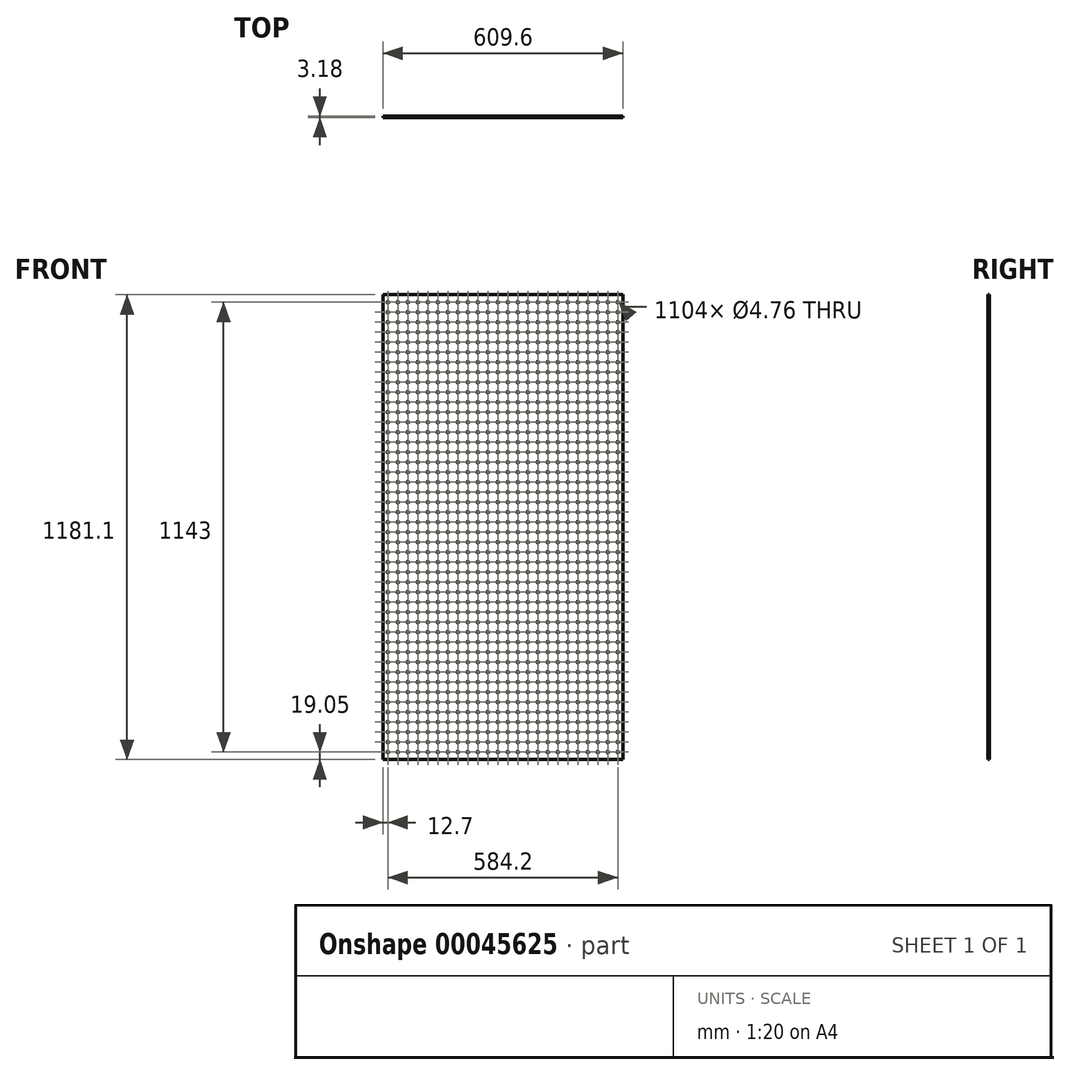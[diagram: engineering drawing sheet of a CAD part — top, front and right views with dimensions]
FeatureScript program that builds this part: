
annotation { "Feature Type Name" : "Feature", "Feature Type Description" : "" }
export const myFeature = defineFeature(function(context is Context, id is Id, definition is map)
    precondition{}
    {
        {
            var Q0;
            Q0=qCreatedBy(makeId("Front.planeOp"),FACE);
            var sketch = newSketch(context, id + "F0", { "sketchPlane" : qUnion([Q0])});
            skLineSegment(sketch, "E0.bottom", {"start": v(-609.6, 0) * mm, "end": v(0, 0) * mm});
            skLineSegment(sketch, "E0.top", {"start": v(-609.6, -1181.1) * mm, "end": v(0, -1181.1) * mm});
            skLineSegment(sketch, "E0.left", {"start": v(-609.6, 0) * mm, "end": v(-609.6, -1181.1) * mm});
            skLineSegment(sketch, "E0.right", {"start": v(0, 0) * mm, "end": v(0, -1181.1) * mm});
            skCircle(sketch, "E1", {"center": v(-596.9, -19.05) * mm, "radius": 2.38 * mm});
            skCircle(sketch, "E2.0.1.0", {"center": v(-596.9, -44.45) * mm, "radius": 2.38 * mm});
            skCircle(sketch, "E2.0.2.0", {"center": v(-596.9, -69.85) * mm, "radius": 2.38 * mm});
            skCircle(sketch, "E2.0.3.0", {"center": v(-596.9, -95.25) * mm, "radius": 2.38 * mm});
            skCircle(sketch, "E2.0.4.0", {"center": v(-596.9, -120.65) * mm, "radius": 2.38 * mm});
            skCircle(sketch, "E2.0.5.0", {"center": v(-596.9, -146.05) * mm, "radius": 2.38 * mm});
            skCircle(sketch, "E2.0.6.0", {"center": v(-596.9, -171.45) * mm, "radius": 2.38 * mm});
            skCircle(sketch, "E2.0.7.0", {"center": v(-596.9, -196.85) * mm, "radius": 2.38 * mm});
            skCircle(sketch, "E2.0.8.0", {"center": v(-596.9, -222.25) * mm, "radius": 2.38 * mm});
            skCircle(sketch, "E2.0.9.0", {"center": v(-596.9, -247.65) * mm, "radius": 2.38 * mm});
            skCircle(sketch, "E2.1.0.0", {"center": v(-571.5, -19.05) * mm, "radius": 2.38 * mm});
            skCircle(sketch, "E2.1.1.0", {"center": v(-571.5, -44.45) * mm, "radius": 2.38 * mm});
            skCircle(sketch, "E2.1.2.0", {"center": v(-571.5, -69.85) * mm, "radius": 2.38 * mm});
            skCircle(sketch, "E2.1.3.0", {"center": v(-571.5, -95.25) * mm, "radius": 2.38 * mm});
            skCircle(sketch, "E2.1.4.0", {"center": v(-571.5, -120.65) * mm, "radius": 2.38 * mm});
            skCircle(sketch, "E2.1.5.0", {"center": v(-571.5, -146.05) * mm, "radius": 2.38 * mm});
            skCircle(sketch, "E2.1.6.0", {"center": v(-571.5, -171.45) * mm, "radius": 2.38 * mm});
            skCircle(sketch, "E2.1.7.0", {"center": v(-571.5, -196.85) * mm, "radius": 2.38 * mm});
            skCircle(sketch, "E2.1.8.0", {"center": v(-571.5, -222.25) * mm, "radius": 2.38 * mm});
            skCircle(sketch, "E2.1.9.0", {"center": v(-571.5, -247.65) * mm, "radius": 2.38 * mm});
            skCircle(sketch, "E2.2.0.0", {"center": v(-546.1, -19.05) * mm, "radius": 2.38 * mm});
            skCircle(sketch, "E2.2.1.0", {"center": v(-546.1, -44.45) * mm, "radius": 2.38 * mm});
            skCircle(sketch, "E2.2.2.0", {"center": v(-546.1, -69.85) * mm, "radius": 2.38 * mm});
            skCircle(sketch, "E2.2.3.0", {"center": v(-546.1, -95.25) * mm, "radius": 2.38 * mm});
            skCircle(sketch, "E2.2.4.0", {"center": v(-546.1, -120.65) * mm, "radius": 2.38 * mm});
            skCircle(sketch, "E2.2.5.0", {"center": v(-546.1, -146.05) * mm, "radius": 2.38 * mm});
            skCircle(sketch, "E2.2.6.0", {"center": v(-546.1, -171.45) * mm, "radius": 2.38 * mm});
            skCircle(sketch, "E2.2.7.0", {"center": v(-546.1, -196.85) * mm, "radius": 2.38 * mm});
            skCircle(sketch, "E2.2.8.0", {"center": v(-546.1, -222.25) * mm, "radius": 2.38 * mm});
            skCircle(sketch, "E2.2.9.0", {"center": v(-546.1, -247.65) * mm, "radius": 2.38 * mm});
            skCircle(sketch, "E2.3.0.0", {"center": v(-520.7, -19.05) * mm, "radius": 2.38 * mm});
            skCircle(sketch, "E2.3.1.0", {"center": v(-520.7, -44.45) * mm, "radius": 2.38 * mm});
            skCircle(sketch, "E2.3.2.0", {"center": v(-520.7, -69.85) * mm, "radius": 2.38 * mm});
            skCircle(sketch, "E2.3.3.0", {"center": v(-520.7, -95.25) * mm, "radius": 2.38 * mm});
            skCircle(sketch, "E2.3.4.0", {"center": v(-520.7, -120.65) * mm, "radius": 2.38 * mm});
            skCircle(sketch, "E2.3.5.0", {"center": v(-520.7, -146.05) * mm, "radius": 2.38 * mm});
            skCircle(sketch, "E2.3.6.0", {"center": v(-520.7, -171.45) * mm, "radius": 2.38 * mm});
            skCircle(sketch, "E2.3.7.0", {"center": v(-520.7, -196.85) * mm, "radius": 2.38 * mm});
            skCircle(sketch, "E2.3.8.0", {"center": v(-520.7, -222.25) * mm, "radius": 2.38 * mm});
            skCircle(sketch, "E2.3.9.0", {"center": v(-520.7, -247.65) * mm, "radius": 2.38 * mm});
            skCircle(sketch, "E2.4.0.0", {"center": v(-495.3, -19.05) * mm, "radius": 2.38 * mm});
            skCircle(sketch, "E2.4.1.0", {"center": v(-495.3, -44.45) * mm, "radius": 2.38 * mm});
            skCircle(sketch, "E2.4.2.0", {"center": v(-495.3, -69.85) * mm, "radius": 2.38 * mm});
            skCircle(sketch, "E2.4.3.0", {"center": v(-495.3, -95.25) * mm, "radius": 2.38 * mm});
            skCircle(sketch, "E2.4.4.0", {"center": v(-495.3, -120.65) * mm, "radius": 2.38 * mm});
            skCircle(sketch, "E2.4.5.0", {"center": v(-495.3, -146.05) * mm, "radius": 2.38 * mm});
            skCircle(sketch, "E2.4.6.0", {"center": v(-495.3, -171.45) * mm, "radius": 2.38 * mm});
            skCircle(sketch, "E2.4.7.0", {"center": v(-495.3, -196.85) * mm, "radius": 2.38 * mm});
            skCircle(sketch, "E2.4.8.0", {"center": v(-495.3, -222.25) * mm, "radius": 2.38 * mm});
            skCircle(sketch, "E2.4.9.0", {"center": v(-495.3, -247.65) * mm, "radius": 2.38 * mm});
            skCircle(sketch, "E2.5.0.0", {"center": v(-469.9, -19.05) * mm, "radius": 2.38 * mm});
            skCircle(sketch, "E2.5.1.0", {"center": v(-469.9, -44.45) * mm, "radius": 2.38 * mm});
            skCircle(sketch, "E2.5.2.0", {"center": v(-469.9, -69.85) * mm, "radius": 2.38 * mm});
            skCircle(sketch, "E2.5.3.0", {"center": v(-469.9, -95.25) * mm, "radius": 2.38 * mm});
            skCircle(sketch, "E2.5.4.0", {"center": v(-469.9, -120.65) * mm, "radius": 2.38 * mm});
            skCircle(sketch, "E2.5.5.0", {"center": v(-469.9, -146.05) * mm, "radius": 2.38 * mm});
            skCircle(sketch, "E2.5.6.0", {"center": v(-469.9, -171.45) * mm, "radius": 2.38 * mm});
            skCircle(sketch, "E2.5.7.0", {"center": v(-469.9, -196.85) * mm, "radius": 2.38 * mm});
            skCircle(sketch, "E2.5.8.0", {"center": v(-469.9, -222.25) * mm, "radius": 2.38 * mm});
            skCircle(sketch, "E2.5.9.0", {"center": v(-469.9, -247.65) * mm, "radius": 2.38 * mm});
            skCircle(sketch, "E2.6.0.0", {"center": v(-444.5, -19.05) * mm, "radius": 2.38 * mm});
            skCircle(sketch, "E2.6.1.0", {"center": v(-444.5, -44.45) * mm, "radius": 2.38 * mm});
            skCircle(sketch, "E2.6.2.0", {"center": v(-444.5, -69.85) * mm, "radius": 2.38 * mm});
            skCircle(sketch, "E2.6.3.0", {"center": v(-444.5, -95.25) * mm, "radius": 2.38 * mm});
            skCircle(sketch, "E2.6.4.0", {"center": v(-444.5, -120.65) * mm, "radius": 2.38 * mm});
            skCircle(sketch, "E2.6.5.0", {"center": v(-444.5, -146.05) * mm, "radius": 2.38 * mm});
            skCircle(sketch, "E2.6.6.0", {"center": v(-444.5, -171.45) * mm, "radius": 2.38 * mm});
            skCircle(sketch, "E2.6.7.0", {"center": v(-444.5, -196.85) * mm, "radius": 2.38 * mm});
            skCircle(sketch, "E2.6.8.0", {"center": v(-444.5, -222.25) * mm, "radius": 2.38 * mm});
            skCircle(sketch, "E2.6.9.0", {"center": v(-444.5, -247.65) * mm, "radius": 2.38 * mm});
            skCircle(sketch, "E2.7.0.0", {"center": v(-419.1, -19.05) * mm, "radius": 2.38 * mm});
            skCircle(sketch, "E2.7.1.0", {"center": v(-419.1, -44.45) * mm, "radius": 2.38 * mm});
            skCircle(sketch, "E2.7.2.0", {"center": v(-419.1, -69.85) * mm, "radius": 2.38 * mm});
            skCircle(sketch, "E2.7.3.0", {"center": v(-419.1, -95.25) * mm, "radius": 2.38 * mm});
            skCircle(sketch, "E2.7.4.0", {"center": v(-419.1, -120.65) * mm, "radius": 2.38 * mm});
            skCircle(sketch, "E2.7.5.0", {"center": v(-419.1, -146.05) * mm, "radius": 2.38 * mm});
            skCircle(sketch, "E2.7.6.0", {"center": v(-419.1, -171.45) * mm, "radius": 2.38 * mm});
            skCircle(sketch, "E2.7.7.0", {"center": v(-419.1, -196.85) * mm, "radius": 2.38 * mm});
            skCircle(sketch, "E2.7.8.0", {"center": v(-419.1, -222.25) * mm, "radius": 2.38 * mm});
            skCircle(sketch, "E2.7.9.0", {"center": v(-419.1, -247.65) * mm, "radius": 2.38 * mm});
            skCircle(sketch, "E2.8.0.0", {"center": v(-393.7, -19.05) * mm, "radius": 2.38 * mm});
            skCircle(sketch, "E2.8.1.0", {"center": v(-393.7, -44.45) * mm, "radius": 2.38 * mm});
            skCircle(sketch, "E2.8.2.0", {"center": v(-393.7, -69.85) * mm, "radius": 2.38 * mm});
            skCircle(sketch, "E2.8.3.0", {"center": v(-393.7, -95.25) * mm, "radius": 2.38 * mm});
            skCircle(sketch, "E2.8.4.0", {"center": v(-393.7, -120.65) * mm, "radius": 2.38 * mm});
            skCircle(sketch, "E2.8.5.0", {"center": v(-393.7, -146.05) * mm, "radius": 2.38 * mm});
            skCircle(sketch, "E2.8.6.0", {"center": v(-393.7, -171.45) * mm, "radius": 2.38 * mm});
            skCircle(sketch, "E2.8.7.0", {"center": v(-393.7, -196.85) * mm, "radius": 2.38 * mm});
            skCircle(sketch, "E2.8.8.0", {"center": v(-393.7, -222.25) * mm, "radius": 2.38 * mm});
            skCircle(sketch, "E2.8.9.0", {"center": v(-393.7, -247.65) * mm, "radius": 2.38 * mm});
            skCircle(sketch, "E2.9.0.0", {"center": v(-368.3, -19.05) * mm, "radius": 2.38 * mm});
            skCircle(sketch, "E2.9.1.0", {"center": v(-368.3, -44.45) * mm, "radius": 2.38 * mm});
            skCircle(sketch, "E2.9.2.0", {"center": v(-368.3, -69.85) * mm, "radius": 2.38 * mm});
            skCircle(sketch, "E2.9.3.0", {"center": v(-368.3, -95.25) * mm, "radius": 2.38 * mm});
            skCircle(sketch, "E2.9.4.0", {"center": v(-368.3, -120.65) * mm, "radius": 2.38 * mm});
            skCircle(sketch, "E2.9.5.0", {"center": v(-368.3, -146.05) * mm, "radius": 2.38 * mm});
            skCircle(sketch, "E2.9.6.0", {"center": v(-368.3, -171.45) * mm, "radius": 2.38 * mm});
            skCircle(sketch, "E2.9.7.0", {"center": v(-368.3, -196.85) * mm, "radius": 2.38 * mm});
            skCircle(sketch, "E2.9.8.0", {"center": v(-368.3, -222.25) * mm, "radius": 2.38 * mm});
            skCircle(sketch, "E2.9.9.0", {"center": v(-368.3, -247.65) * mm, "radius": 2.38 * mm});
            skLineSegment(sketch, "E2.direction1", {"start": v(-596.9, -19.05) * mm, "end": v(-571.5, -19.05) * mm, "construction": true});
            skLineSegment(sketch, "E2.direction2", {"start": v(-596.9, -19.05) * mm, "end": v(-596.9, -44.45) * mm, "construction": true});
            skCircle(sketch, "E3.0.10.0", {"center": v(-342.9, -19.05) * mm, "radius": 2.38 * mm});
            skCircle(sketch, "E3.0.10.1", {"center": v(-342.9, -44.45) * mm, "radius": 2.38 * mm});
            skCircle(sketch, "E3.0.10.2", {"center": v(-342.9, -69.85) * mm, "radius": 2.38 * mm});
            skCircle(sketch, "E3.0.10.3", {"center": v(-342.9, -95.25) * mm, "radius": 2.38 * mm});
            skCircle(sketch, "E3.0.10.4", {"center": v(-342.9, -120.65) * mm, "radius": 2.38 * mm});
            skCircle(sketch, "E3.0.10.5", {"center": v(-342.9, -146.05) * mm, "radius": 2.38 * mm});
            skCircle(sketch, "E3.0.10.6", {"center": v(-342.9, -171.45) * mm, "radius": 2.38 * mm});
            skCircle(sketch, "E3.0.10.7", {"center": v(-342.9, -196.85) * mm, "radius": 2.38 * mm});
            skCircle(sketch, "E3.0.10.8", {"center": v(-342.9, -222.25) * mm, "radius": 2.38 * mm});
            skCircle(sketch, "E3.0.10.9", {"center": v(-342.9, -247.65) * mm, "radius": 2.38 * mm});
            skCircle(sketch, "E3.0.11.0", {"center": v(-317.5, -19.05) * mm, "radius": 2.38 * mm});
            skCircle(sketch, "E3.0.11.1", {"center": v(-317.5, -44.45) * mm, "radius": 2.38 * mm});
            skCircle(sketch, "E3.0.11.2", {"center": v(-317.5, -69.85) * mm, "radius": 2.38 * mm});
            skCircle(sketch, "E3.0.11.3", {"center": v(-317.5, -95.25) * mm, "radius": 2.38 * mm});
            skCircle(sketch, "E3.0.11.4", {"center": v(-317.5, -120.65) * mm, "radius": 2.38 * mm});
            skCircle(sketch, "E3.0.11.5", {"center": v(-317.5, -146.05) * mm, "radius": 2.38 * mm});
            skCircle(sketch, "E3.0.11.6", {"center": v(-317.5, -171.45) * mm, "radius": 2.38 * mm});
            skCircle(sketch, "E3.0.11.7", {"center": v(-317.5, -196.85) * mm, "radius": 2.38 * mm});
            skCircle(sketch, "E3.0.11.8", {"center": v(-317.5, -222.25) * mm, "radius": 2.38 * mm});
            skCircle(sketch, "E3.0.11.9", {"center": v(-317.5, -247.65) * mm, "radius": 2.38 * mm});
            skCircle(sketch, "E3.0.12.0", {"center": v(-292.1, -19.05) * mm, "radius": 2.38 * mm});
            skCircle(sketch, "E3.0.12.1", {"center": v(-292.1, -44.45) * mm, "radius": 2.38 * mm});
            skCircle(sketch, "E3.0.12.2", {"center": v(-292.1, -69.85) * mm, "radius": 2.38 * mm});
            skCircle(sketch, "E3.0.12.3", {"center": v(-292.1, -95.25) * mm, "radius": 2.38 * mm});
            skCircle(sketch, "E3.0.12.4", {"center": v(-292.1, -120.65) * mm, "radius": 2.38 * mm});
            skCircle(sketch, "E3.0.12.5", {"center": v(-292.1, -146.05) * mm, "radius": 2.38 * mm});
            skCircle(sketch, "E3.0.12.6", {"center": v(-292.1, -171.45) * mm, "radius": 2.38 * mm});
            skCircle(sketch, "E3.0.12.7", {"center": v(-292.1, -196.85) * mm, "radius": 2.38 * mm});
            skCircle(sketch, "E3.0.12.8", {"center": v(-292.1, -222.25) * mm, "radius": 2.38 * mm});
            skCircle(sketch, "E3.0.12.9", {"center": v(-292.1, -247.65) * mm, "radius": 2.38 * mm});
            skCircle(sketch, "E3.0.13.0", {"center": v(-266.7, -19.05) * mm, "radius": 2.38 * mm});
            skCircle(sketch, "E3.0.13.1", {"center": v(-266.7, -44.45) * mm, "radius": 2.38 * mm});
            skCircle(sketch, "E3.0.13.2", {"center": v(-266.7, -69.85) * mm, "radius": 2.38 * mm});
            skCircle(sketch, "E3.0.13.3", {"center": v(-266.7, -95.25) * mm, "radius": 2.38 * mm});
            skCircle(sketch, "E3.0.13.4", {"center": v(-266.7, -120.65) * mm, "radius": 2.38 * mm});
            skCircle(sketch, "E3.0.13.5", {"center": v(-266.7, -146.05) * mm, "radius": 2.38 * mm});
            skCircle(sketch, "E3.0.13.6", {"center": v(-266.7, -171.45) * mm, "radius": 2.38 * mm});
            skCircle(sketch, "E3.0.13.7", {"center": v(-266.7, -196.85) * mm, "radius": 2.38 * mm});
            skCircle(sketch, "E3.0.13.8", {"center": v(-266.7, -222.25) * mm, "radius": 2.38 * mm});
            skCircle(sketch, "E3.0.13.9", {"center": v(-266.7, -247.65) * mm, "radius": 2.38 * mm});
            skCircle(sketch, "E3.0.14.0", {"center": v(-241.3, -19.05) * mm, "radius": 2.38 * mm});
            skCircle(sketch, "E3.0.14.1", {"center": v(-241.3, -44.45) * mm, "radius": 2.38 * mm});
            skCircle(sketch, "E3.0.14.2", {"center": v(-241.3, -69.85) * mm, "radius": 2.38 * mm});
            skCircle(sketch, "E3.0.14.3", {"center": v(-241.3, -95.25) * mm, "radius": 2.38 * mm});
            skCircle(sketch, "E3.0.14.4", {"center": v(-241.3, -120.65) * mm, "radius": 2.38 * mm});
            skCircle(sketch, "E3.0.14.5", {"center": v(-241.3, -146.05) * mm, "radius": 2.38 * mm});
            skCircle(sketch, "E3.0.14.6", {"center": v(-241.3, -171.45) * mm, "radius": 2.38 * mm});
            skCircle(sketch, "E3.0.14.7", {"center": v(-241.3, -196.85) * mm, "radius": 2.38 * mm});
            skCircle(sketch, "E3.0.14.8", {"center": v(-241.3, -222.25) * mm, "radius": 2.38 * mm});
            skCircle(sketch, "E3.0.14.9", {"center": v(-241.3, -247.65) * mm, "radius": 2.38 * mm});
            skCircle(sketch, "E4.0.15.0", {"center": v(-215.9, -19.05) * mm, "radius": 2.38 * mm});
            skCircle(sketch, "E4.0.15.1", {"center": v(-215.9, -44.45) * mm, "radius": 2.38 * mm});
            skCircle(sketch, "E4.0.15.2", {"center": v(-215.9, -69.85) * mm, "radius": 2.38 * mm});
            skCircle(sketch, "E4.0.15.3", {"center": v(-215.9, -95.25) * mm, "radius": 2.38 * mm});
            skCircle(sketch, "E4.0.15.4", {"center": v(-215.9, -120.65) * mm, "radius": 2.38 * mm});
            skCircle(sketch, "E4.0.15.5", {"center": v(-215.9, -146.05) * mm, "radius": 2.38 * mm});
            skCircle(sketch, "E4.0.15.6", {"center": v(-215.9, -171.45) * mm, "radius": 2.38 * mm});
            skCircle(sketch, "E4.0.15.7", {"center": v(-215.9, -196.85) * mm, "radius": 2.38 * mm});
            skCircle(sketch, "E4.0.15.8", {"center": v(-215.9, -222.25) * mm, "radius": 2.38 * mm});
            skCircle(sketch, "E4.0.15.9", {"center": v(-215.9, -247.65) * mm, "radius": 2.38 * mm});
            skCircle(sketch, "E4.0.16.0", {"center": v(-190.5, -19.05) * mm, "radius": 2.38 * mm});
            skCircle(sketch, "E4.0.16.1", {"center": v(-190.5, -44.45) * mm, "radius": 2.38 * mm});
            skCircle(sketch, "E4.0.16.2", {"center": v(-190.5, -69.85) * mm, "radius": 2.38 * mm});
            skCircle(sketch, "E4.0.16.3", {"center": v(-190.5, -95.25) * mm, "radius": 2.38 * mm});
            skCircle(sketch, "E4.0.16.4", {"center": v(-190.5, -120.65) * mm, "radius": 2.38 * mm});
            skCircle(sketch, "E4.0.16.5", {"center": v(-190.5, -146.05) * mm, "radius": 2.38 * mm});
            skCircle(sketch, "E4.0.16.6", {"center": v(-190.5, -171.45) * mm, "radius": 2.38 * mm});
            skCircle(sketch, "E4.0.16.7", {"center": v(-190.5, -196.85) * mm, "radius": 2.38 * mm});
            skCircle(sketch, "E4.0.16.8", {"center": v(-190.5, -222.25) * mm, "radius": 2.38 * mm});
            skCircle(sketch, "E4.0.16.9", {"center": v(-190.5, -247.65) * mm, "radius": 2.38 * mm});
            skCircle(sketch, "E4.0.17.0", {"center": v(-165.1, -19.05) * mm, "radius": 2.38 * mm});
            skCircle(sketch, "E4.0.17.1", {"center": v(-165.1, -44.45) * mm, "radius": 2.38 * mm});
            skCircle(sketch, "E4.0.17.2", {"center": v(-165.1, -69.85) * mm, "radius": 2.38 * mm});
            skCircle(sketch, "E4.0.17.3", {"center": v(-165.1, -95.25) * mm, "radius": 2.38 * mm});
            skCircle(sketch, "E4.0.17.4", {"center": v(-165.1, -120.65) * mm, "radius": 2.38 * mm});
            skCircle(sketch, "E4.0.17.5", {"center": v(-165.1, -146.05) * mm, "radius": 2.38 * mm});
            skCircle(sketch, "E4.0.17.6", {"center": v(-165.1, -171.45) * mm, "radius": 2.38 * mm});
            skCircle(sketch, "E4.0.17.7", {"center": v(-165.1, -196.85) * mm, "radius": 2.38 * mm});
            skCircle(sketch, "E4.0.17.8", {"center": v(-165.1, -222.25) * mm, "radius": 2.38 * mm});
            skCircle(sketch, "E4.0.17.9", {"center": v(-165.1, -247.65) * mm, "radius": 2.38 * mm});
            skCircle(sketch, "E4.0.18.0", {"center": v(-139.7, -19.05) * mm, "radius": 2.38 * mm});
            skCircle(sketch, "E4.0.18.1", {"center": v(-139.7, -44.45) * mm, "radius": 2.38 * mm});
            skCircle(sketch, "E4.0.18.2", {"center": v(-139.7, -69.85) * mm, "radius": 2.38 * mm});
            skCircle(sketch, "E4.0.18.3", {"center": v(-139.7, -95.25) * mm, "radius": 2.38 * mm});
            skCircle(sketch, "E4.0.18.4", {"center": v(-139.7, -120.65) * mm, "radius": 2.38 * mm});
            skCircle(sketch, "E4.0.18.5", {"center": v(-139.7, -146.05) * mm, "radius": 2.38 * mm});
            skCircle(sketch, "E4.0.18.6", {"center": v(-139.7, -171.45) * mm, "radius": 2.38 * mm});
            skCircle(sketch, "E4.0.18.7", {"center": v(-139.7, -196.85) * mm, "radius": 2.38 * mm});
            skCircle(sketch, "E4.0.18.8", {"center": v(-139.7, -222.25) * mm, "radius": 2.38 * mm});
            skCircle(sketch, "E4.0.18.9", {"center": v(-139.7, -247.65) * mm, "radius": 2.38 * mm});
            skCircle(sketch, "E4.0.19.0", {"center": v(-114.3, -19.05) * mm, "radius": 2.38 * mm});
            skCircle(sketch, "E4.0.19.1", {"center": v(-114.3, -44.45) * mm, "radius": 2.38 * mm});
            skCircle(sketch, "E4.0.19.2", {"center": v(-114.3, -69.85) * mm, "radius": 2.38 * mm});
            skCircle(sketch, "E4.0.19.3", {"center": v(-114.3, -95.25) * mm, "radius": 2.38 * mm});
            skCircle(sketch, "E4.0.19.4", {"center": v(-114.3, -120.65) * mm, "radius": 2.38 * mm});
            skCircle(sketch, "E4.0.19.5", {"center": v(-114.3, -146.05) * mm, "radius": 2.38 * mm});
            skCircle(sketch, "E4.0.19.6", {"center": v(-114.3, -171.45) * mm, "radius": 2.38 * mm});
            skCircle(sketch, "E4.0.19.7", {"center": v(-114.3, -196.85) * mm, "radius": 2.38 * mm});
            skCircle(sketch, "E4.0.19.8", {"center": v(-114.3, -222.25) * mm, "radius": 2.38 * mm});
            skCircle(sketch, "E4.0.19.9", {"center": v(-114.3, -247.65) * mm, "radius": 2.38 * mm});
            skCircle(sketch, "E4.0.20.0", {"center": v(-88.9, -19.05) * mm, "radius": 2.38 * mm});
            skCircle(sketch, "E4.0.20.1", {"center": v(-88.9, -44.45) * mm, "radius": 2.38 * mm});
            skCircle(sketch, "E4.0.20.2", {"center": v(-88.9, -69.85) * mm, "radius": 2.38 * mm});
            skCircle(sketch, "E4.0.20.3", {"center": v(-88.9, -95.25) * mm, "radius": 2.38 * mm});
            skCircle(sketch, "E4.0.20.4", {"center": v(-88.9, -120.65) * mm, "radius": 2.38 * mm});
            skCircle(sketch, "E4.0.20.5", {"center": v(-88.9, -146.05) * mm, "radius": 2.38 * mm});
            skCircle(sketch, "E4.0.20.6", {"center": v(-88.9, -171.45) * mm, "radius": 2.38 * mm});
            skCircle(sketch, "E4.0.20.7", {"center": v(-88.9, -196.85) * mm, "radius": 2.38 * mm});
            skCircle(sketch, "E4.0.20.8", {"center": v(-88.9, -222.25) * mm, "radius": 2.38 * mm});
            skCircle(sketch, "E4.0.20.9", {"center": v(-88.9, -247.65) * mm, "radius": 2.38 * mm});
            skCircle(sketch, "E4.0.21.0", {"center": v(-63.5, -19.05) * mm, "radius": 2.38 * mm});
            skCircle(sketch, "E4.0.21.1", {"center": v(-63.5, -44.45) * mm, "radius": 2.38 * mm});
            skCircle(sketch, "E4.0.21.2", {"center": v(-63.5, -69.85) * mm, "radius": 2.38 * mm});
            skCircle(sketch, "E4.0.21.3", {"center": v(-63.5, -95.25) * mm, "radius": 2.38 * mm});
            skCircle(sketch, "E4.0.21.4", {"center": v(-63.5, -120.65) * mm, "radius": 2.38 * mm});
            skCircle(sketch, "E4.0.21.5", {"center": v(-63.5, -146.05) * mm, "radius": 2.38 * mm});
            skCircle(sketch, "E4.0.21.6", {"center": v(-63.5, -171.45) * mm, "radius": 2.38 * mm});
            skCircle(sketch, "E4.0.21.7", {"center": v(-63.5, -196.85) * mm, "radius": 2.38 * mm});
            skCircle(sketch, "E4.0.21.8", {"center": v(-63.5, -222.25) * mm, "radius": 2.38 * mm});
            skCircle(sketch, "E4.0.21.9", {"center": v(-63.5, -247.65) * mm, "radius": 2.38 * mm});
            skCircle(sketch, "E5.0.22.0", {"center": v(-38.1, -19.05) * mm, "radius": 2.38 * mm});
            skCircle(sketch, "E5.0.22.1", {"center": v(-38.1, -44.45) * mm, "radius": 2.38 * mm});
            skCircle(sketch, "E5.0.22.2", {"center": v(-38.1, -69.85) * mm, "radius": 2.38 * mm});
            skCircle(sketch, "E5.0.22.3", {"center": v(-38.1, -95.25) * mm, "radius": 2.38 * mm});
            skCircle(sketch, "E5.0.22.4", {"center": v(-38.1, -120.65) * mm, "radius": 2.38 * mm});
            skCircle(sketch, "E5.0.22.5", {"center": v(-38.1, -146.05) * mm, "radius": 2.38 * mm});
            skCircle(sketch, "E5.0.22.6", {"center": v(-38.1, -171.45) * mm, "radius": 2.38 * mm});
            skCircle(sketch, "E5.0.22.7", {"center": v(-38.1, -196.85) * mm, "radius": 2.38 * mm});
            skCircle(sketch, "E5.0.22.8", {"center": v(-38.1, -222.25) * mm, "radius": 2.38 * mm});
            skCircle(sketch, "E5.0.22.9", {"center": v(-38.1, -247.65) * mm, "radius": 2.38 * mm});
            skCircle(sketch, "E6.0.23.0", {"center": v(-12.7, -19.05) * mm, "radius": 2.38 * mm});
            skCircle(sketch, "E6.0.23.1", {"center": v(-12.7, -44.45) * mm, "radius": 2.38 * mm});
            skCircle(sketch, "E6.0.23.2", {"center": v(-12.7, -69.85) * mm, "radius": 2.38 * mm});
            skCircle(sketch, "E6.0.23.3", {"center": v(-12.7, -95.25) * mm, "radius": 2.38 * mm});
            skCircle(sketch, "E6.0.23.4", {"center": v(-12.7, -120.65) * mm, "radius": 2.38 * mm});
            skCircle(sketch, "E6.0.23.5", {"center": v(-12.7, -146.05) * mm, "radius": 2.38 * mm});
            skCircle(sketch, "E6.0.23.6", {"center": v(-12.7, -171.45) * mm, "radius": 2.38 * mm});
            skCircle(sketch, "E6.0.23.7", {"center": v(-12.7, -196.85) * mm, "radius": 2.38 * mm});
            skCircle(sketch, "E6.0.23.8", {"center": v(-12.7, -222.25) * mm, "radius": 2.38 * mm});
            skCircle(sketch, "E6.0.23.9", {"center": v(-12.7, -247.65) * mm, "radius": 2.38 * mm});
            skCircle(sketch, "E7.0.0.10", {"center": v(-596.9, -273.05) * mm, "radius": 2.38 * mm});
            skCircle(sketch, "E7.0.0.11", {"center": v(-596.9, -298.45) * mm, "radius": 2.38 * mm});
            skCircle(sketch, "E7.0.0.12", {"center": v(-596.9, -323.85) * mm, "radius": 2.38 * mm});
            skCircle(sketch, "E7.0.0.13", {"center": v(-596.9, -349.25) * mm, "radius": 2.38 * mm});
            skCircle(sketch, "E7.0.0.14", {"center": v(-596.9, -374.65) * mm, "radius": 2.38 * mm});
            skCircle(sketch, "E7.0.0.15", {"center": v(-596.9, -400.05) * mm, "radius": 2.38 * mm});
            skCircle(sketch, "E7.0.0.16", {"center": v(-596.9, -425.45) * mm, "radius": 2.38 * mm});
            skCircle(sketch, "E7.0.0.17", {"center": v(-596.9, -450.85) * mm, "radius": 2.38 * mm});
            skCircle(sketch, "E7.0.0.18", {"center": v(-596.9, -476.25) * mm, "radius": 2.38 * mm});
            skCircle(sketch, "E7.0.0.19", {"center": v(-596.9, -501.65) * mm, "radius": 2.38 * mm});
            skCircle(sketch, "E7.0.0.20", {"center": v(-596.9, -527.05) * mm, "radius": 2.38 * mm});
            skCircle(sketch, "E7.0.0.21", {"center": v(-596.9, -552.45) * mm, "radius": 2.38 * mm});
            skCircle(sketch, "E7.0.0.22", {"center": v(-596.9, -577.85) * mm, "radius": 2.38 * mm});
            skCircle(sketch, "E7.0.0.23", {"center": v(-596.9, -603.25) * mm, "radius": 2.38 * mm});
            skCircle(sketch, "E7.0.0.24", {"center": v(-596.9, -628.65) * mm, "radius": 2.38 * mm});
            skCircle(sketch, "E7.0.1.10", {"center": v(-571.5, -273.05) * mm, "radius": 2.38 * mm});
            skCircle(sketch, "E7.0.1.11", {"center": v(-571.5, -298.45) * mm, "radius": 2.38 * mm});
            skCircle(sketch, "E7.0.1.12", {"center": v(-571.5, -323.85) * mm, "radius": 2.38 * mm});
            skCircle(sketch, "E7.0.1.13", {"center": v(-571.5, -349.25) * mm, "radius": 2.38 * mm});
            skCircle(sketch, "E7.0.1.14", {"center": v(-571.5, -374.65) * mm, "radius": 2.38 * mm});
            skCircle(sketch, "E7.0.1.15", {"center": v(-571.5, -400.05) * mm, "radius": 2.38 * mm});
            skCircle(sketch, "E7.0.1.16", {"center": v(-571.5, -425.45) * mm, "radius": 2.38 * mm});
            skCircle(sketch, "E7.0.1.17", {"center": v(-571.5, -450.85) * mm, "radius": 2.38 * mm});
            skCircle(sketch, "E7.0.1.18", {"center": v(-571.5, -476.25) * mm, "radius": 2.38 * mm});
            skCircle(sketch, "E7.0.1.19", {"center": v(-571.5, -501.65) * mm, "radius": 2.38 * mm});
            skCircle(sketch, "E7.0.1.20", {"center": v(-571.5, -527.05) * mm, "radius": 2.38 * mm});
            skCircle(sketch, "E7.0.1.21", {"center": v(-571.5, -552.45) * mm, "radius": 2.38 * mm});
            skCircle(sketch, "E7.0.1.22", {"center": v(-571.5, -577.85) * mm, "radius": 2.38 * mm});
            skCircle(sketch, "E7.0.1.23", {"center": v(-571.5, -603.25) * mm, "radius": 2.38 * mm});
            skCircle(sketch, "E7.0.1.24", {"center": v(-571.5, -628.65) * mm, "radius": 2.38 * mm});
            skCircle(sketch, "E7.0.2.10", {"center": v(-546.1, -273.05) * mm, "radius": 2.38 * mm});
            skCircle(sketch, "E7.0.2.11", {"center": v(-546.1, -298.45) * mm, "radius": 2.38 * mm});
            skCircle(sketch, "E7.0.2.12", {"center": v(-546.1, -323.85) * mm, "radius": 2.38 * mm});
            skCircle(sketch, "E7.0.2.13", {"center": v(-546.1, -349.25) * mm, "radius": 2.38 * mm});
            skCircle(sketch, "E7.0.2.14", {"center": v(-546.1, -374.65) * mm, "radius": 2.38 * mm});
            skCircle(sketch, "E7.0.2.15", {"center": v(-546.1, -400.05) * mm, "radius": 2.38 * mm});
            skCircle(sketch, "E7.0.2.16", {"center": v(-546.1, -425.45) * mm, "radius": 2.38 * mm});
            skCircle(sketch, "E7.0.2.17", {"center": v(-546.1, -450.85) * mm, "radius": 2.38 * mm});
            skCircle(sketch, "E7.0.2.18", {"center": v(-546.1, -476.25) * mm, "radius": 2.38 * mm});
            skCircle(sketch, "E7.0.2.19", {"center": v(-546.1, -501.65) * mm, "radius": 2.38 * mm});
            skCircle(sketch, "E7.0.2.20", {"center": v(-546.1, -527.05) * mm, "radius": 2.38 * mm});
            skCircle(sketch, "E7.0.2.21", {"center": v(-546.1, -552.45) * mm, "radius": 2.38 * mm});
            skCircle(sketch, "E7.0.2.22", {"center": v(-546.1, -577.85) * mm, "radius": 2.38 * mm});
            skCircle(sketch, "E7.0.2.23", {"center": v(-546.1, -603.25) * mm, "radius": 2.38 * mm});
            skCircle(sketch, "E7.0.2.24", {"center": v(-546.1, -628.65) * mm, "radius": 2.38 * mm});
            skCircle(sketch, "E7.0.3.10", {"center": v(-520.7, -273.05) * mm, "radius": 2.38 * mm});
            skCircle(sketch, "E7.0.3.11", {"center": v(-520.7, -298.45) * mm, "radius": 2.38 * mm});
            skCircle(sketch, "E7.0.3.12", {"center": v(-520.7, -323.85) * mm, "radius": 2.38 * mm});
            skCircle(sketch, "E7.0.3.13", {"center": v(-520.7, -349.25) * mm, "radius": 2.38 * mm});
            skCircle(sketch, "E7.0.3.14", {"center": v(-520.7, -374.65) * mm, "radius": 2.38 * mm});
            skCircle(sketch, "E7.0.3.15", {"center": v(-520.7, -400.05) * mm, "radius": 2.38 * mm});
            skCircle(sketch, "E7.0.3.16", {"center": v(-520.7, -425.45) * mm, "radius": 2.38 * mm});
            skCircle(sketch, "E7.0.3.17", {"center": v(-520.7, -450.85) * mm, "radius": 2.38 * mm});
            skCircle(sketch, "E7.0.3.18", {"center": v(-520.7, -476.25) * mm, "radius": 2.38 * mm});
            skCircle(sketch, "E7.0.3.19", {"center": v(-520.7, -501.65) * mm, "radius": 2.38 * mm});
            skCircle(sketch, "E7.0.3.20", {"center": v(-520.7, -527.05) * mm, "radius": 2.38 * mm});
            skCircle(sketch, "E7.0.3.21", {"center": v(-520.7, -552.45) * mm, "radius": 2.38 * mm});
            skCircle(sketch, "E7.0.3.22", {"center": v(-520.7, -577.85) * mm, "radius": 2.38 * mm});
            skCircle(sketch, "E7.0.3.23", {"center": v(-520.7, -603.25) * mm, "radius": 2.38 * mm});
            skCircle(sketch, "E7.0.3.24", {"center": v(-520.7, -628.65) * mm, "radius": 2.38 * mm});
            skCircle(sketch, "E7.0.4.10", {"center": v(-495.3, -273.05) * mm, "radius": 2.38 * mm});
            skCircle(sketch, "E7.0.4.11", {"center": v(-495.3, -298.45) * mm, "radius": 2.38 * mm});
            skCircle(sketch, "E7.0.4.12", {"center": v(-495.3, -323.85) * mm, "radius": 2.38 * mm});
            skCircle(sketch, "E7.0.4.13", {"center": v(-495.3, -349.25) * mm, "radius": 2.38 * mm});
            skCircle(sketch, "E7.0.4.14", {"center": v(-495.3, -374.65) * mm, "radius": 2.38 * mm});
            skCircle(sketch, "E7.0.4.15", {"center": v(-495.3, -400.05) * mm, "radius": 2.38 * mm});
            skCircle(sketch, "E7.0.4.16", {"center": v(-495.3, -425.45) * mm, "radius": 2.38 * mm});
            skCircle(sketch, "E7.0.4.17", {"center": v(-495.3, -450.85) * mm, "radius": 2.38 * mm});
            skCircle(sketch, "E7.0.4.18", {"center": v(-495.3, -476.25) * mm, "radius": 2.38 * mm});
            skCircle(sketch, "E7.0.4.19", {"center": v(-495.3, -501.65) * mm, "radius": 2.38 * mm});
            skCircle(sketch, "E7.0.4.20", {"center": v(-495.3, -527.05) * mm, "radius": 2.38 * mm});
            skCircle(sketch, "E7.0.4.21", {"center": v(-495.3, -552.45) * mm, "radius": 2.38 * mm});
            skCircle(sketch, "E7.0.4.22", {"center": v(-495.3, -577.85) * mm, "radius": 2.38 * mm});
            skCircle(sketch, "E7.0.4.23", {"center": v(-495.3, -603.25) * mm, "radius": 2.38 * mm});
            skCircle(sketch, "E7.0.4.24", {"center": v(-495.3, -628.65) * mm, "radius": 2.38 * mm});
            skCircle(sketch, "E7.0.5.10", {"center": v(-469.9, -273.05) * mm, "radius": 2.38 * mm});
            skCircle(sketch, "E7.0.5.11", {"center": v(-469.9, -298.45) * mm, "radius": 2.38 * mm});
            skCircle(sketch, "E7.0.5.12", {"center": v(-469.9, -323.85) * mm, "radius": 2.38 * mm});
            skCircle(sketch, "E7.0.5.13", {"center": v(-469.9, -349.25) * mm, "radius": 2.38 * mm});
            skCircle(sketch, "E7.0.5.14", {"center": v(-469.9, -374.65) * mm, "radius": 2.38 * mm});
            skCircle(sketch, "E7.0.5.15", {"center": v(-469.9, -400.05) * mm, "radius": 2.38 * mm});
            skCircle(sketch, "E7.0.5.16", {"center": v(-469.9, -425.45) * mm, "radius": 2.38 * mm});
            skCircle(sketch, "E7.0.5.17", {"center": v(-469.9, -450.85) * mm, "radius": 2.38 * mm});
            skCircle(sketch, "E7.0.5.18", {"center": v(-469.9, -476.25) * mm, "radius": 2.38 * mm});
            skCircle(sketch, "E7.0.5.19", {"center": v(-469.9, -501.65) * mm, "radius": 2.38 * mm});
            skCircle(sketch, "E7.0.5.20", {"center": v(-469.9, -527.05) * mm, "radius": 2.38 * mm});
            skCircle(sketch, "E7.0.5.21", {"center": v(-469.9, -552.45) * mm, "radius": 2.38 * mm});
            skCircle(sketch, "E7.0.5.22", {"center": v(-469.9, -577.85) * mm, "radius": 2.38 * mm});
            skCircle(sketch, "E7.0.5.23", {"center": v(-469.9, -603.25) * mm, "radius": 2.38 * mm});
            skCircle(sketch, "E7.0.5.24", {"center": v(-469.9, -628.65) * mm, "radius": 2.38 * mm});
            skCircle(sketch, "E7.0.6.10", {"center": v(-444.5, -273.05) * mm, "radius": 2.38 * mm});
            skCircle(sketch, "E7.0.6.11", {"center": v(-444.5, -298.45) * mm, "radius": 2.38 * mm});
            skCircle(sketch, "E7.0.6.12", {"center": v(-444.5, -323.85) * mm, "radius": 2.38 * mm});
            skCircle(sketch, "E7.0.6.13", {"center": v(-444.5, -349.25) * mm, "radius": 2.38 * mm});
            skCircle(sketch, "E7.0.6.14", {"center": v(-444.5, -374.65) * mm, "radius": 2.38 * mm});
            skCircle(sketch, "E7.0.6.15", {"center": v(-444.5, -400.05) * mm, "radius": 2.38 * mm});
            skCircle(sketch, "E7.0.6.16", {"center": v(-444.5, -425.45) * mm, "radius": 2.38 * mm});
            skCircle(sketch, "E7.0.6.17", {"center": v(-444.5, -450.85) * mm, "radius": 2.38 * mm});
            skCircle(sketch, "E7.0.6.18", {"center": v(-444.5, -476.25) * mm, "radius": 2.38 * mm});
            skCircle(sketch, "E7.0.6.19", {"center": v(-444.5, -501.65) * mm, "radius": 2.38 * mm});
            skCircle(sketch, "E7.0.6.20", {"center": v(-444.5, -527.05) * mm, "radius": 2.38 * mm});
            skCircle(sketch, "E7.0.6.21", {"center": v(-444.5, -552.45) * mm, "radius": 2.38 * mm});
            skCircle(sketch, "E7.0.6.22", {"center": v(-444.5, -577.85) * mm, "radius": 2.38 * mm});
            skCircle(sketch, "E7.0.6.23", {"center": v(-444.5, -603.25) * mm, "radius": 2.38 * mm});
            skCircle(sketch, "E7.0.6.24", {"center": v(-444.5, -628.65) * mm, "radius": 2.38 * mm});
            skCircle(sketch, "E7.0.7.10", {"center": v(-419.1, -273.05) * mm, "radius": 2.38 * mm});
            skCircle(sketch, "E7.0.7.11", {"center": v(-419.1, -298.45) * mm, "radius": 2.38 * mm});
            skCircle(sketch, "E7.0.7.12", {"center": v(-419.1, -323.85) * mm, "radius": 2.38 * mm});
            skCircle(sketch, "E7.0.7.13", {"center": v(-419.1, -349.25) * mm, "radius": 2.38 * mm});
            skCircle(sketch, "E7.0.7.14", {"center": v(-419.1, -374.65) * mm, "radius": 2.38 * mm});
            skCircle(sketch, "E7.0.7.15", {"center": v(-419.1, -400.05) * mm, "radius": 2.38 * mm});
            skCircle(sketch, "E7.0.7.16", {"center": v(-419.1, -425.45) * mm, "radius": 2.38 * mm});
            skCircle(sketch, "E7.0.7.17", {"center": v(-419.1, -450.85) * mm, "radius": 2.38 * mm});
            skCircle(sketch, "E7.0.7.18", {"center": v(-419.1, -476.25) * mm, "radius": 2.38 * mm});
            skCircle(sketch, "E7.0.7.19", {"center": v(-419.1, -501.65) * mm, "radius": 2.38 * mm});
            skCircle(sketch, "E7.0.7.20", {"center": v(-419.1, -527.05) * mm, "radius": 2.38 * mm});
            skCircle(sketch, "E7.0.7.21", {"center": v(-419.1, -552.45) * mm, "radius": 2.38 * mm});
            skCircle(sketch, "E7.0.7.22", {"center": v(-419.1, -577.85) * mm, "radius": 2.38 * mm});
            skCircle(sketch, "E7.0.7.23", {"center": v(-419.1, -603.25) * mm, "radius": 2.38 * mm});
            skCircle(sketch, "E7.0.7.24", {"center": v(-419.1, -628.65) * mm, "radius": 2.38 * mm});
            skCircle(sketch, "E7.0.8.10", {"center": v(-393.7, -273.05) * mm, "radius": 2.38 * mm});
            skCircle(sketch, "E7.0.8.11", {"center": v(-393.7, -298.45) * mm, "radius": 2.38 * mm});
            skCircle(sketch, "E7.0.8.12", {"center": v(-393.7, -323.85) * mm, "radius": 2.38 * mm});
            skCircle(sketch, "E7.0.8.13", {"center": v(-393.7, -349.25) * mm, "radius": 2.38 * mm});
            skCircle(sketch, "E7.0.8.14", {"center": v(-393.7, -374.65) * mm, "radius": 2.38 * mm});
            skCircle(sketch, "E7.0.8.15", {"center": v(-393.7, -400.05) * mm, "radius": 2.38 * mm});
            skCircle(sketch, "E7.0.8.16", {"center": v(-393.7, -425.45) * mm, "radius": 2.38 * mm});
            skCircle(sketch, "E7.0.8.17", {"center": v(-393.7, -450.85) * mm, "radius": 2.38 * mm});
            skCircle(sketch, "E7.0.8.18", {"center": v(-393.7, -476.25) * mm, "radius": 2.38 * mm});
            skCircle(sketch, "E7.0.8.19", {"center": v(-393.7, -501.65) * mm, "radius": 2.38 * mm});
            skCircle(sketch, "E7.0.8.20", {"center": v(-393.7, -527.05) * mm, "radius": 2.38 * mm});
            skCircle(sketch, "E7.0.8.21", {"center": v(-393.7, -552.45) * mm, "radius": 2.38 * mm});
            skCircle(sketch, "E7.0.8.22", {"center": v(-393.7, -577.85) * mm, "radius": 2.38 * mm});
            skCircle(sketch, "E7.0.8.23", {"center": v(-393.7, -603.25) * mm, "radius": 2.38 * mm});
            skCircle(sketch, "E7.0.8.24", {"center": v(-393.7, -628.65) * mm, "radius": 2.38 * mm});
            skCircle(sketch, "E7.0.9.10", {"center": v(-368.3, -273.05) * mm, "radius": 2.38 * mm});
            skCircle(sketch, "E7.0.9.11", {"center": v(-368.3, -298.45) * mm, "radius": 2.38 * mm});
            skCircle(sketch, "E7.0.9.12", {"center": v(-368.3, -323.85) * mm, "radius": 2.38 * mm});
            skCircle(sketch, "E7.0.9.13", {"center": v(-368.3, -349.25) * mm, "radius": 2.38 * mm});
            skCircle(sketch, "E7.0.9.14", {"center": v(-368.3, -374.65) * mm, "radius": 2.38 * mm});
            skCircle(sketch, "E7.0.9.15", {"center": v(-368.3, -400.05) * mm, "radius": 2.38 * mm});
            skCircle(sketch, "E7.0.9.16", {"center": v(-368.3, -425.45) * mm, "radius": 2.38 * mm});
            skCircle(sketch, "E7.0.9.17", {"center": v(-368.3, -450.85) * mm, "radius": 2.38 * mm});
            skCircle(sketch, "E7.0.9.18", {"center": v(-368.3, -476.25) * mm, "radius": 2.38 * mm});
            skCircle(sketch, "E7.0.9.19", {"center": v(-368.3, -501.65) * mm, "radius": 2.38 * mm});
            skCircle(sketch, "E7.0.9.20", {"center": v(-368.3, -527.05) * mm, "radius": 2.38 * mm});
            skCircle(sketch, "E7.0.9.21", {"center": v(-368.3, -552.45) * mm, "radius": 2.38 * mm});
            skCircle(sketch, "E7.0.9.22", {"center": v(-368.3, -577.85) * mm, "radius": 2.38 * mm});
            skCircle(sketch, "E7.0.9.23", {"center": v(-368.3, -603.25) * mm, "radius": 2.38 * mm});
            skCircle(sketch, "E7.0.9.24", {"center": v(-368.3, -628.65) * mm, "radius": 2.38 * mm});
            skCircle(sketch, "E7.0.10.10", {"center": v(-342.9, -273.05) * mm, "radius": 2.38 * mm});
            skCircle(sketch, "E7.0.10.11", {"center": v(-342.9, -298.45) * mm, "radius": 2.38 * mm});
            skCircle(sketch, "E7.0.10.12", {"center": v(-342.9, -323.85) * mm, "radius": 2.38 * mm});
            skCircle(sketch, "E7.0.10.13", {"center": v(-342.9, -349.25) * mm, "radius": 2.38 * mm});
            skCircle(sketch, "E7.0.10.14", {"center": v(-342.9, -374.65) * mm, "radius": 2.38 * mm});
            skCircle(sketch, "E7.0.10.15", {"center": v(-342.9, -400.05) * mm, "radius": 2.38 * mm});
            skCircle(sketch, "E7.0.10.16", {"center": v(-342.9, -425.45) * mm, "radius": 2.38 * mm});
            skCircle(sketch, "E7.0.10.17", {"center": v(-342.9, -450.85) * mm, "radius": 2.38 * mm});
            skCircle(sketch, "E7.0.10.18", {"center": v(-342.9, -476.25) * mm, "radius": 2.38 * mm});
            skCircle(sketch, "E7.0.10.19", {"center": v(-342.9, -501.65) * mm, "radius": 2.38 * mm});
            skCircle(sketch, "E7.0.10.20", {"center": v(-342.9, -527.05) * mm, "radius": 2.38 * mm});
            skCircle(sketch, "E7.0.10.21", {"center": v(-342.9, -552.45) * mm, "radius": 2.38 * mm});
            skCircle(sketch, "E7.0.10.22", {"center": v(-342.9, -577.85) * mm, "radius": 2.38 * mm});
            skCircle(sketch, "E7.0.10.23", {"center": v(-342.9, -603.25) * mm, "radius": 2.38 * mm});
            skCircle(sketch, "E7.0.10.24", {"center": v(-342.9, -628.65) * mm, "radius": 2.38 * mm});
            skCircle(sketch, "E7.0.11.10", {"center": v(-317.5, -273.05) * mm, "radius": 2.38 * mm});
            skCircle(sketch, "E7.0.11.11", {"center": v(-317.5, -298.45) * mm, "radius": 2.38 * mm});
            skCircle(sketch, "E7.0.11.12", {"center": v(-317.5, -323.85) * mm, "radius": 2.38 * mm});
            skCircle(sketch, "E7.0.11.13", {"center": v(-317.5, -349.25) * mm, "radius": 2.38 * mm});
            skCircle(sketch, "E7.0.11.14", {"center": v(-317.5, -374.65) * mm, "radius": 2.38 * mm});
            skCircle(sketch, "E7.0.11.15", {"center": v(-317.5, -400.05) * mm, "radius": 2.38 * mm});
            skCircle(sketch, "E7.0.11.16", {"center": v(-317.5, -425.45) * mm, "radius": 2.38 * mm});
            skCircle(sketch, "E7.0.11.17", {"center": v(-317.5, -450.85) * mm, "radius": 2.38 * mm});
            skCircle(sketch, "E7.0.11.18", {"center": v(-317.5, -476.25) * mm, "radius": 2.38 * mm});
            skCircle(sketch, "E7.0.11.19", {"center": v(-317.5, -501.65) * mm, "radius": 2.38 * mm});
            skCircle(sketch, "E7.0.11.20", {"center": v(-317.5, -527.05) * mm, "radius": 2.38 * mm});
            skCircle(sketch, "E7.0.11.21", {"center": v(-317.5, -552.45) * mm, "radius": 2.38 * mm});
            skCircle(sketch, "E7.0.11.22", {"center": v(-317.5, -577.85) * mm, "radius": 2.38 * mm});
            skCircle(sketch, "E7.0.11.23", {"center": v(-317.5, -603.25) * mm, "radius": 2.38 * mm});
            skCircle(sketch, "E7.0.11.24", {"center": v(-317.5, -628.65) * mm, "radius": 2.38 * mm});
            skCircle(sketch, "E7.0.12.10", {"center": v(-292.1, -273.05) * mm, "radius": 2.38 * mm});
            skCircle(sketch, "E7.0.12.11", {"center": v(-292.1, -298.45) * mm, "radius": 2.38 * mm});
            skCircle(sketch, "E7.0.12.12", {"center": v(-292.1, -323.85) * mm, "radius": 2.38 * mm});
            skCircle(sketch, "E7.0.12.13", {"center": v(-292.1, -349.25) * mm, "radius": 2.38 * mm});
            skCircle(sketch, "E7.0.12.14", {"center": v(-292.1, -374.65) * mm, "radius": 2.38 * mm});
            skCircle(sketch, "E7.0.12.15", {"center": v(-292.1, -400.05) * mm, "radius": 2.38 * mm});
            skCircle(sketch, "E7.0.12.16", {"center": v(-292.1, -425.45) * mm, "radius": 2.38 * mm});
            skCircle(sketch, "E7.0.12.17", {"center": v(-292.1, -450.85) * mm, "radius": 2.38 * mm});
            skCircle(sketch, "E7.0.12.18", {"center": v(-292.1, -476.25) * mm, "radius": 2.38 * mm});
            skCircle(sketch, "E7.0.12.19", {"center": v(-292.1, -501.65) * mm, "radius": 2.38 * mm});
            skCircle(sketch, "E7.0.12.20", {"center": v(-292.1, -527.05) * mm, "radius": 2.38 * mm});
            skCircle(sketch, "E7.0.12.21", {"center": v(-292.1, -552.45) * mm, "radius": 2.38 * mm});
            skCircle(sketch, "E7.0.12.22", {"center": v(-292.1, -577.85) * mm, "radius": 2.38 * mm});
            skCircle(sketch, "E7.0.12.23", {"center": v(-292.1, -603.25) * mm, "radius": 2.38 * mm});
            skCircle(sketch, "E7.0.12.24", {"center": v(-292.1, -628.65) * mm, "radius": 2.38 * mm});
            skCircle(sketch, "E7.0.13.10", {"center": v(-266.7, -273.05) * mm, "radius": 2.38 * mm});
            skCircle(sketch, "E7.0.13.11", {"center": v(-266.7, -298.45) * mm, "radius": 2.38 * mm});
            skCircle(sketch, "E7.0.13.12", {"center": v(-266.7, -323.85) * mm, "radius": 2.38 * mm});
            skCircle(sketch, "E7.0.13.13", {"center": v(-266.7, -349.25) * mm, "radius": 2.38 * mm});
            skCircle(sketch, "E7.0.13.14", {"center": v(-266.7, -374.65) * mm, "radius": 2.38 * mm});
            skCircle(sketch, "E7.0.13.15", {"center": v(-266.7, -400.05) * mm, "radius": 2.38 * mm});
            skCircle(sketch, "E7.0.13.16", {"center": v(-266.7, -425.45) * mm, "radius": 2.38 * mm});
            skCircle(sketch, "E7.0.13.17", {"center": v(-266.7, -450.85) * mm, "radius": 2.38 * mm});
            skCircle(sketch, "E7.0.13.18", {"center": v(-266.7, -476.25) * mm, "radius": 2.38 * mm});
            skCircle(sketch, "E7.0.13.19", {"center": v(-266.7, -501.65) * mm, "radius": 2.38 * mm});
            skCircle(sketch, "E7.0.13.20", {"center": v(-266.7, -527.05) * mm, "radius": 2.38 * mm});
            skCircle(sketch, "E7.0.13.21", {"center": v(-266.7, -552.45) * mm, "radius": 2.38 * mm});
            skCircle(sketch, "E7.0.13.22", {"center": v(-266.7, -577.85) * mm, "radius": 2.38 * mm});
            skCircle(sketch, "E7.0.13.23", {"center": v(-266.7, -603.25) * mm, "radius": 2.38 * mm});
            skCircle(sketch, "E7.0.13.24", {"center": v(-266.7, -628.65) * mm, "radius": 2.38 * mm});
            skCircle(sketch, "E7.0.14.10", {"center": v(-241.3, -273.05) * mm, "radius": 2.38 * mm});
            skCircle(sketch, "E7.0.14.11", {"center": v(-241.3, -298.45) * mm, "radius": 2.38 * mm});
            skCircle(sketch, "E7.0.14.12", {"center": v(-241.3, -323.85) * mm, "radius": 2.38 * mm});
            skCircle(sketch, "E7.0.14.13", {"center": v(-241.3, -349.25) * mm, "radius": 2.38 * mm});
            skCircle(sketch, "E7.0.14.14", {"center": v(-241.3, -374.65) * mm, "radius": 2.38 * mm});
            skCircle(sketch, "E7.0.14.15", {"center": v(-241.3, -400.05) * mm, "radius": 2.38 * mm});
            skCircle(sketch, "E7.0.14.16", {"center": v(-241.3, -425.45) * mm, "radius": 2.38 * mm});
            skCircle(sketch, "E7.0.14.17", {"center": v(-241.3, -450.85) * mm, "radius": 2.38 * mm});
            skCircle(sketch, "E7.0.14.18", {"center": v(-241.3, -476.25) * mm, "radius": 2.38 * mm});
            skCircle(sketch, "E7.0.14.19", {"center": v(-241.3, -501.65) * mm, "radius": 2.38 * mm});
            skCircle(sketch, "E7.0.14.20", {"center": v(-241.3, -527.05) * mm, "radius": 2.38 * mm});
            skCircle(sketch, "E7.0.14.21", {"center": v(-241.3, -552.45) * mm, "radius": 2.38 * mm});
            skCircle(sketch, "E7.0.14.22", {"center": v(-241.3, -577.85) * mm, "radius": 2.38 * mm});
            skCircle(sketch, "E7.0.14.23", {"center": v(-241.3, -603.25) * mm, "radius": 2.38 * mm});
            skCircle(sketch, "E7.0.14.24", {"center": v(-241.3, -628.65) * mm, "radius": 2.38 * mm});
            skCircle(sketch, "E7.0.15.10", {"center": v(-215.9, -273.05) * mm, "radius": 2.38 * mm});
            skCircle(sketch, "E7.0.15.11", {"center": v(-215.9, -298.45) * mm, "radius": 2.38 * mm});
            skCircle(sketch, "E7.0.15.12", {"center": v(-215.9, -323.85) * mm, "radius": 2.38 * mm});
            skCircle(sketch, "E7.0.15.13", {"center": v(-215.9, -349.25) * mm, "radius": 2.38 * mm});
            skCircle(sketch, "E7.0.15.14", {"center": v(-215.9, -374.65) * mm, "radius": 2.38 * mm});
            skCircle(sketch, "E7.0.15.15", {"center": v(-215.9, -400.05) * mm, "radius": 2.38 * mm});
            skCircle(sketch, "E7.0.15.16", {"center": v(-215.9, -425.45) * mm, "radius": 2.38 * mm});
            skCircle(sketch, "E7.0.15.17", {"center": v(-215.9, -450.85) * mm, "radius": 2.38 * mm});
            skCircle(sketch, "E7.0.15.18", {"center": v(-215.9, -476.25) * mm, "radius": 2.38 * mm});
            skCircle(sketch, "E7.0.15.19", {"center": v(-215.9, -501.65) * mm, "radius": 2.38 * mm});
            skCircle(sketch, "E7.0.15.20", {"center": v(-215.9, -527.05) * mm, "radius": 2.38 * mm});
            skCircle(sketch, "E7.0.15.21", {"center": v(-215.9, -552.45) * mm, "radius": 2.38 * mm});
            skCircle(sketch, "E7.0.15.22", {"center": v(-215.9, -577.85) * mm, "radius": 2.38 * mm});
            skCircle(sketch, "E7.0.15.23", {"center": v(-215.9, -603.25) * mm, "radius": 2.38 * mm});
            skCircle(sketch, "E7.0.15.24", {"center": v(-215.9, -628.65) * mm, "radius": 2.38 * mm});
            skCircle(sketch, "E7.0.16.10", {"center": v(-190.5, -273.05) * mm, "radius": 2.38 * mm});
            skCircle(sketch, "E7.0.16.11", {"center": v(-190.5, -298.45) * mm, "radius": 2.38 * mm});
            skCircle(sketch, "E7.0.16.12", {"center": v(-190.5, -323.85) * mm, "radius": 2.38 * mm});
            skCircle(sketch, "E7.0.16.13", {"center": v(-190.5, -349.25) * mm, "radius": 2.38 * mm});
            skCircle(sketch, "E7.0.16.14", {"center": v(-190.5, -374.65) * mm, "radius": 2.38 * mm});
            skCircle(sketch, "E7.0.16.15", {"center": v(-190.5, -400.05) * mm, "radius": 2.38 * mm});
            skCircle(sketch, "E7.0.16.16", {"center": v(-190.5, -425.45) * mm, "radius": 2.38 * mm});
            skCircle(sketch, "E7.0.16.17", {"center": v(-190.5, -450.85) * mm, "radius": 2.38 * mm});
            skCircle(sketch, "E7.0.16.18", {"center": v(-190.5, -476.25) * mm, "radius": 2.38 * mm});
            skCircle(sketch, "E7.0.16.19", {"center": v(-190.5, -501.65) * mm, "radius": 2.38 * mm});
            skCircle(sketch, "E7.0.16.20", {"center": v(-190.5, -527.05) * mm, "radius": 2.38 * mm});
            skCircle(sketch, "E7.0.16.21", {"center": v(-190.5, -552.45) * mm, "radius": 2.38 * mm});
            skCircle(sketch, "E7.0.16.22", {"center": v(-190.5, -577.85) * mm, "radius": 2.38 * mm});
            skCircle(sketch, "E7.0.16.23", {"center": v(-190.5, -603.25) * mm, "radius": 2.38 * mm});
            skCircle(sketch, "E7.0.16.24", {"center": v(-190.5, -628.65) * mm, "radius": 2.38 * mm});
            skCircle(sketch, "E7.0.17.10", {"center": v(-165.1, -273.05) * mm, "radius": 2.38 * mm});
            skCircle(sketch, "E7.0.17.11", {"center": v(-165.1, -298.45) * mm, "radius": 2.38 * mm});
            skCircle(sketch, "E7.0.17.12", {"center": v(-165.1, -323.85) * mm, "radius": 2.38 * mm});
            skCircle(sketch, "E7.0.17.13", {"center": v(-165.1, -349.25) * mm, "radius": 2.38 * mm});
            skCircle(sketch, "E7.0.17.14", {"center": v(-165.1, -374.65) * mm, "radius": 2.38 * mm});
            skCircle(sketch, "E7.0.17.15", {"center": v(-165.1, -400.05) * mm, "radius": 2.38 * mm});
            skCircle(sketch, "E7.0.17.16", {"center": v(-165.1, -425.45) * mm, "radius": 2.38 * mm});
            skCircle(sketch, "E7.0.17.17", {"center": v(-165.1, -450.85) * mm, "radius": 2.38 * mm});
            skCircle(sketch, "E7.0.17.18", {"center": v(-165.1, -476.25) * mm, "radius": 2.38 * mm});
            skCircle(sketch, "E7.0.17.19", {"center": v(-165.1, -501.65) * mm, "radius": 2.38 * mm});
            skCircle(sketch, "E7.0.17.20", {"center": v(-165.1, -527.05) * mm, "radius": 2.38 * mm});
            skCircle(sketch, "E7.0.17.21", {"center": v(-165.1, -552.45) * mm, "radius": 2.38 * mm});
            skCircle(sketch, "E7.0.17.22", {"center": v(-165.1, -577.85) * mm, "radius": 2.38 * mm});
            skCircle(sketch, "E7.0.17.23", {"center": v(-165.1, -603.25) * mm, "radius": 2.38 * mm});
            skCircle(sketch, "E7.0.17.24", {"center": v(-165.1, -628.65) * mm, "radius": 2.38 * mm});
            skCircle(sketch, "E7.0.18.10", {"center": v(-139.7, -273.05) * mm, "radius": 2.38 * mm});
            skCircle(sketch, "E7.0.18.11", {"center": v(-139.7, -298.45) * mm, "radius": 2.38 * mm});
            skCircle(sketch, "E7.0.18.12", {"center": v(-139.7, -323.85) * mm, "radius": 2.38 * mm});
            skCircle(sketch, "E7.0.18.13", {"center": v(-139.7, -349.25) * mm, "radius": 2.38 * mm});
            skCircle(sketch, "E7.0.18.14", {"center": v(-139.7, -374.65) * mm, "radius": 2.38 * mm});
            skCircle(sketch, "E7.0.18.15", {"center": v(-139.7, -400.05) * mm, "radius": 2.38 * mm});
            skCircle(sketch, "E7.0.18.16", {"center": v(-139.7, -425.45) * mm, "radius": 2.38 * mm});
            skCircle(sketch, "E7.0.18.17", {"center": v(-139.7, -450.85) * mm, "radius": 2.38 * mm});
            skCircle(sketch, "E7.0.18.18", {"center": v(-139.7, -476.25) * mm, "radius": 2.38 * mm});
            skCircle(sketch, "E7.0.18.19", {"center": v(-139.7, -501.65) * mm, "radius": 2.38 * mm});
            skCircle(sketch, "E7.0.18.20", {"center": v(-139.7, -527.05) * mm, "radius": 2.38 * mm});
            skCircle(sketch, "E7.0.18.21", {"center": v(-139.7, -552.45) * mm, "radius": 2.38 * mm});
            skCircle(sketch, "E7.0.18.22", {"center": v(-139.7, -577.85) * mm, "radius": 2.38 * mm});
            skCircle(sketch, "E7.0.18.23", {"center": v(-139.7, -603.25) * mm, "radius": 2.38 * mm});
            skCircle(sketch, "E7.0.18.24", {"center": v(-139.7, -628.65) * mm, "radius": 2.38 * mm});
            skCircle(sketch, "E7.0.19.10", {"center": v(-114.3, -273.05) * mm, "radius": 2.38 * mm});
            skCircle(sketch, "E7.0.19.11", {"center": v(-114.3, -298.45) * mm, "radius": 2.38 * mm});
            skCircle(sketch, "E7.0.19.12", {"center": v(-114.3, -323.85) * mm, "radius": 2.38 * mm});
            skCircle(sketch, "E7.0.19.13", {"center": v(-114.3, -349.25) * mm, "radius": 2.38 * mm});
            skCircle(sketch, "E7.0.19.14", {"center": v(-114.3, -374.65) * mm, "radius": 2.38 * mm});
            skCircle(sketch, "E7.0.19.15", {"center": v(-114.3, -400.05) * mm, "radius": 2.38 * mm});
            skCircle(sketch, "E7.0.19.16", {"center": v(-114.3, -425.45) * mm, "radius": 2.38 * mm});
            skCircle(sketch, "E7.0.19.17", {"center": v(-114.3, -450.85) * mm, "radius": 2.38 * mm});
            skCircle(sketch, "E7.0.19.18", {"center": v(-114.3, -476.25) * mm, "radius": 2.38 * mm});
            skCircle(sketch, "E7.0.19.19", {"center": v(-114.3, -501.65) * mm, "radius": 2.38 * mm});
            skCircle(sketch, "E7.0.19.20", {"center": v(-114.3, -527.05) * mm, "radius": 2.38 * mm});
            skCircle(sketch, "E7.0.19.21", {"center": v(-114.3, -552.45) * mm, "radius": 2.38 * mm});
            skCircle(sketch, "E7.0.19.22", {"center": v(-114.3, -577.85) * mm, "radius": 2.38 * mm});
            skCircle(sketch, "E7.0.19.23", {"center": v(-114.3, -603.25) * mm, "radius": 2.38 * mm});
            skCircle(sketch, "E7.0.19.24", {"center": v(-114.3, -628.65) * mm, "radius": 2.38 * mm});
            skCircle(sketch, "E7.0.20.10", {"center": v(-88.9, -273.05) * mm, "radius": 2.38 * mm});
            skCircle(sketch, "E7.0.20.11", {"center": v(-88.9, -298.45) * mm, "radius": 2.38 * mm});
            skCircle(sketch, "E7.0.20.12", {"center": v(-88.9, -323.85) * mm, "radius": 2.38 * mm});
            skCircle(sketch, "E7.0.20.13", {"center": v(-88.9, -349.25) * mm, "radius": 2.38 * mm});
            skCircle(sketch, "E7.0.20.14", {"center": v(-88.9, -374.65) * mm, "radius": 2.38 * mm});
            skCircle(sketch, "E7.0.20.15", {"center": v(-88.9, -400.05) * mm, "radius": 2.38 * mm});
            skCircle(sketch, "E7.0.20.16", {"center": v(-88.9, -425.45) * mm, "radius": 2.38 * mm});
            skCircle(sketch, "E7.0.20.17", {"center": v(-88.9, -450.85) * mm, "radius": 2.38 * mm});
            skCircle(sketch, "E7.0.20.18", {"center": v(-88.9, -476.25) * mm, "radius": 2.38 * mm});
            skCircle(sketch, "E7.0.20.19", {"center": v(-88.9, -501.65) * mm, "radius": 2.38 * mm});
            skCircle(sketch, "E7.0.20.20", {"center": v(-88.9, -527.05) * mm, "radius": 2.38 * mm});
            skCircle(sketch, "E7.0.20.21", {"center": v(-88.9, -552.45) * mm, "radius": 2.38 * mm});
            skCircle(sketch, "E7.0.20.22", {"center": v(-88.9, -577.85) * mm, "radius": 2.38 * mm});
            skCircle(sketch, "E7.0.20.23", {"center": v(-88.9, -603.25) * mm, "radius": 2.38 * mm});
            skCircle(sketch, "E7.0.20.24", {"center": v(-88.9, -628.65) * mm, "radius": 2.38 * mm});
            skCircle(sketch, "E7.0.21.10", {"center": v(-63.5, -273.05) * mm, "radius": 2.38 * mm});
            skCircle(sketch, "E7.0.21.11", {"center": v(-63.5, -298.45) * mm, "radius": 2.38 * mm});
            skCircle(sketch, "E7.0.21.12", {"center": v(-63.5, -323.85) * mm, "radius": 2.38 * mm});
            skCircle(sketch, "E7.0.21.13", {"center": v(-63.5, -349.25) * mm, "radius": 2.38 * mm});
            skCircle(sketch, "E7.0.21.14", {"center": v(-63.5, -374.65) * mm, "radius": 2.38 * mm});
            skCircle(sketch, "E7.0.21.15", {"center": v(-63.5, -400.05) * mm, "radius": 2.38 * mm});
            skCircle(sketch, "E7.0.21.16", {"center": v(-63.5, -425.45) * mm, "radius": 2.38 * mm});
            skCircle(sketch, "E7.0.21.17", {"center": v(-63.5, -450.85) * mm, "radius": 2.38 * mm});
            skCircle(sketch, "E7.0.21.18", {"center": v(-63.5, -476.25) * mm, "radius": 2.38 * mm});
            skCircle(sketch, "E7.0.21.19", {"center": v(-63.5, -501.65) * mm, "radius": 2.38 * mm});
            skCircle(sketch, "E7.0.21.20", {"center": v(-63.5, -527.05) * mm, "radius": 2.38 * mm});
            skCircle(sketch, "E7.0.21.21", {"center": v(-63.5, -552.45) * mm, "radius": 2.38 * mm});
            skCircle(sketch, "E7.0.21.22", {"center": v(-63.5, -577.85) * mm, "radius": 2.38 * mm});
            skCircle(sketch, "E7.0.21.23", {"center": v(-63.5, -603.25) * mm, "radius": 2.38 * mm});
            skCircle(sketch, "E7.0.21.24", {"center": v(-63.5, -628.65) * mm, "radius": 2.38 * mm});
            skCircle(sketch, "E7.0.22.10", {"center": v(-38.1, -273.05) * mm, "radius": 2.38 * mm});
            skCircle(sketch, "E7.0.22.11", {"center": v(-38.1, -298.45) * mm, "radius": 2.38 * mm});
            skCircle(sketch, "E7.0.22.12", {"center": v(-38.1, -323.85) * mm, "radius": 2.38 * mm});
            skCircle(sketch, "E7.0.22.13", {"center": v(-38.1, -349.25) * mm, "radius": 2.38 * mm});
            skCircle(sketch, "E7.0.22.14", {"center": v(-38.1, -374.65) * mm, "radius": 2.38 * mm});
            skCircle(sketch, "E7.0.22.15", {"center": v(-38.1, -400.05) * mm, "radius": 2.38 * mm});
            skCircle(sketch, "E7.0.22.16", {"center": v(-38.1, -425.45) * mm, "radius": 2.38 * mm});
            skCircle(sketch, "E7.0.22.17", {"center": v(-38.1, -450.85) * mm, "radius": 2.38 * mm});
            skCircle(sketch, "E7.0.22.18", {"center": v(-38.1, -476.25) * mm, "radius": 2.38 * mm});
            skCircle(sketch, "E7.0.22.19", {"center": v(-38.1, -501.65) * mm, "radius": 2.38 * mm});
            skCircle(sketch, "E7.0.22.20", {"center": v(-38.1, -527.05) * mm, "radius": 2.38 * mm});
            skCircle(sketch, "E7.0.22.21", {"center": v(-38.1, -552.45) * mm, "radius": 2.38 * mm});
            skCircle(sketch, "E7.0.22.22", {"center": v(-38.1, -577.85) * mm, "radius": 2.38 * mm});
            skCircle(sketch, "E7.0.22.23", {"center": v(-38.1, -603.25) * mm, "radius": 2.38 * mm});
            skCircle(sketch, "E7.0.22.24", {"center": v(-38.1, -628.65) * mm, "radius": 2.38 * mm});
            skCircle(sketch, "E7.0.23.10", {"center": v(-12.7, -273.05) * mm, "radius": 2.38 * mm});
            skCircle(sketch, "E7.0.23.11", {"center": v(-12.7, -298.45) * mm, "radius": 2.38 * mm});
            skCircle(sketch, "E7.0.23.12", {"center": v(-12.7, -323.85) * mm, "radius": 2.38 * mm});
            skCircle(sketch, "E7.0.23.13", {"center": v(-12.7, -349.25) * mm, "radius": 2.38 * mm});
            skCircle(sketch, "E7.0.23.14", {"center": v(-12.7, -374.65) * mm, "radius": 2.38 * mm});
            skCircle(sketch, "E7.0.23.15", {"center": v(-12.7, -400.05) * mm, "radius": 2.38 * mm});
            skCircle(sketch, "E7.0.23.16", {"center": v(-12.7, -425.45) * mm, "radius": 2.38 * mm});
            skCircle(sketch, "E7.0.23.17", {"center": v(-12.7, -450.85) * mm, "radius": 2.38 * mm});
            skCircle(sketch, "E7.0.23.18", {"center": v(-12.7, -476.25) * mm, "radius": 2.38 * mm});
            skCircle(sketch, "E7.0.23.19", {"center": v(-12.7, -501.65) * mm, "radius": 2.38 * mm});
            skCircle(sketch, "E7.0.23.20", {"center": v(-12.7, -527.05) * mm, "radius": 2.38 * mm});
            skCircle(sketch, "E7.0.23.21", {"center": v(-12.7, -552.45) * mm, "radius": 2.38 * mm});
            skCircle(sketch, "E7.0.23.22", {"center": v(-12.7, -577.85) * mm, "radius": 2.38 * mm});
            skCircle(sketch, "E7.0.23.23", {"center": v(-12.7, -603.25) * mm, "radius": 2.38 * mm});
            skCircle(sketch, "E7.0.23.24", {"center": v(-12.7, -628.65) * mm, "radius": 2.38 * mm});
            skCircle(sketch, "E8.0.0.25", {"center": v(-596.9, -654.05) * mm, "radius": 2.38 * mm});
            skCircle(sketch, "E8.0.0.26", {"center": v(-596.9, -679.45) * mm, "radius": 2.38 * mm});
            skCircle(sketch, "E8.0.0.27", {"center": v(-596.9, -704.85) * mm, "radius": 2.38 * mm});
            skCircle(sketch, "E8.0.0.28", {"center": v(-596.9, -730.25) * mm, "radius": 2.38 * mm});
            skCircle(sketch, "E8.0.0.29", {"center": v(-596.9, -755.65) * mm, "radius": 2.38 * mm});
            skCircle(sketch, "E8.0.0.30", {"center": v(-596.9, -781.05) * mm, "radius": 2.38 * mm});
            skCircle(sketch, "E8.0.0.31", {"center": v(-596.9, -806.45) * mm, "radius": 2.38 * mm});
            skCircle(sketch, "E8.0.0.32", {"center": v(-596.9, -831.85) * mm, "radius": 2.38 * mm});
            skCircle(sketch, "E8.0.0.33", {"center": v(-596.9, -857.25) * mm, "radius": 2.38 * mm});
            skCircle(sketch, "E8.0.0.34", {"center": v(-596.9, -882.65) * mm, "radius": 2.38 * mm});
            skCircle(sketch, "E8.0.0.35", {"center": v(-596.9, -908.05) * mm, "radius": 2.38 * mm});
            skCircle(sketch, "E8.0.0.36", {"center": v(-596.9, -933.45) * mm, "radius": 2.38 * mm});
            skCircle(sketch, "E8.0.0.37", {"center": v(-596.9, -958.85) * mm, "radius": 2.38 * mm});
            skCircle(sketch, "E8.0.0.38", {"center": v(-596.9, -984.25) * mm, "radius": 2.38 * mm});
            skCircle(sketch, "E8.0.0.39", {"center": v(-596.9, -1009.65) * mm, "radius": 2.38 * mm});
            skCircle(sketch, "E8.0.0.40", {"center": v(-596.9, -1035.05) * mm, "radius": 2.38 * mm});
            skCircle(sketch, "E8.0.0.41", {"center": v(-596.9, -1060.45) * mm, "radius": 2.38 * mm});
            skCircle(sketch, "E8.0.0.42", {"center": v(-596.9, -1085.85) * mm, "radius": 2.38 * mm});
            skCircle(sketch, "E8.0.0.43", {"center": v(-596.9, -1111.25) * mm, "radius": 2.38 * mm});
            skCircle(sketch, "E8.0.0.44", {"center": v(-596.9, -1136.65) * mm, "radius": 2.38 * mm});
            skCircle(sketch, "E8.0.0.45", {"center": v(-596.9, -1162.05) * mm, "radius": 2.38 * mm});
            skCircle(sketch, "E8.0.1.25", {"center": v(-571.5, -654.05) * mm, "radius": 2.38 * mm});
            skCircle(sketch, "E8.0.1.26", {"center": v(-571.5, -679.45) * mm, "radius": 2.38 * mm});
            skCircle(sketch, "E8.0.1.27", {"center": v(-571.5, -704.85) * mm, "radius": 2.38 * mm});
            skCircle(sketch, "E8.0.1.28", {"center": v(-571.5, -730.25) * mm, "radius": 2.38 * mm});
            skCircle(sketch, "E8.0.1.29", {"center": v(-571.5, -755.65) * mm, "radius": 2.38 * mm});
            skCircle(sketch, "E8.0.1.30", {"center": v(-571.5, -781.05) * mm, "radius": 2.38 * mm});
            skCircle(sketch, "E8.0.1.31", {"center": v(-571.5, -806.45) * mm, "radius": 2.38 * mm});
            skCircle(sketch, "E8.0.1.32", {"center": v(-571.5, -831.85) * mm, "radius": 2.38 * mm});
            skCircle(sketch, "E8.0.1.33", {"center": v(-571.5, -857.25) * mm, "radius": 2.38 * mm});
            skCircle(sketch, "E8.0.1.34", {"center": v(-571.5, -882.65) * mm, "radius": 2.38 * mm});
            skCircle(sketch, "E8.0.1.35", {"center": v(-571.5, -908.05) * mm, "radius": 2.38 * mm});
            skCircle(sketch, "E8.0.1.36", {"center": v(-571.5, -933.45) * mm, "radius": 2.38 * mm});
            skCircle(sketch, "E8.0.1.37", {"center": v(-571.5, -958.85) * mm, "radius": 2.38 * mm});
            skCircle(sketch, "E8.0.1.38", {"center": v(-571.5, -984.25) * mm, "radius": 2.38 * mm});
            skCircle(sketch, "E8.0.1.39", {"center": v(-571.5, -1009.65) * mm, "radius": 2.38 * mm});
            skCircle(sketch, "E8.0.1.40", {"center": v(-571.5, -1035.05) * mm, "radius": 2.38 * mm});
            skCircle(sketch, "E8.0.1.41", {"center": v(-571.5, -1060.45) * mm, "radius": 2.38 * mm});
            skCircle(sketch, "E8.0.1.42", {"center": v(-571.5, -1085.85) * mm, "radius": 2.38 * mm});
            skCircle(sketch, "E8.0.1.43", {"center": v(-571.5, -1111.25) * mm, "radius": 2.38 * mm});
            skCircle(sketch, "E8.0.1.44", {"center": v(-571.5, -1136.65) * mm, "radius": 2.38 * mm});
            skCircle(sketch, "E8.0.1.45", {"center": v(-571.5, -1162.05) * mm, "radius": 2.38 * mm});
            skCircle(sketch, "E8.0.2.25", {"center": v(-546.1, -654.05) * mm, "radius": 2.38 * mm});
            skCircle(sketch, "E8.0.2.26", {"center": v(-546.1, -679.45) * mm, "radius": 2.38 * mm});
            skCircle(sketch, "E8.0.2.27", {"center": v(-546.1, -704.85) * mm, "radius": 2.38 * mm});
            skCircle(sketch, "E8.0.2.28", {"center": v(-546.1, -730.25) * mm, "radius": 2.38 * mm});
            skCircle(sketch, "E8.0.2.29", {"center": v(-546.1, -755.65) * mm, "radius": 2.38 * mm});
            skCircle(sketch, "E8.0.2.30", {"center": v(-546.1, -781.05) * mm, "radius": 2.38 * mm});
            skCircle(sketch, "E8.0.2.31", {"center": v(-546.1, -806.45) * mm, "radius": 2.38 * mm});
            skCircle(sketch, "E8.0.2.32", {"center": v(-546.1, -831.85) * mm, "radius": 2.38 * mm});
            skCircle(sketch, "E8.0.2.33", {"center": v(-546.1, -857.25) * mm, "radius": 2.38 * mm});
            skCircle(sketch, "E8.0.2.34", {"center": v(-546.1, -882.65) * mm, "radius": 2.38 * mm});
            skCircle(sketch, "E8.0.2.35", {"center": v(-546.1, -908.05) * mm, "radius": 2.38 * mm});
            skCircle(sketch, "E8.0.2.36", {"center": v(-546.1, -933.45) * mm, "radius": 2.38 * mm});
            skCircle(sketch, "E8.0.2.37", {"center": v(-546.1, -958.85) * mm, "radius": 2.38 * mm});
            skCircle(sketch, "E8.0.2.38", {"center": v(-546.1, -984.25) * mm, "radius": 2.38 * mm});
            skCircle(sketch, "E8.0.2.39", {"center": v(-546.1, -1009.65) * mm, "radius": 2.38 * mm});
            skCircle(sketch, "E8.0.2.40", {"center": v(-546.1, -1035.05) * mm, "radius": 2.38 * mm});
            skCircle(sketch, "E8.0.2.41", {"center": v(-546.1, -1060.45) * mm, "radius": 2.38 * mm});
            skCircle(sketch, "E8.0.2.42", {"center": v(-546.1, -1085.85) * mm, "radius": 2.38 * mm});
            skCircle(sketch, "E8.0.2.43", {"center": v(-546.1, -1111.25) * mm, "radius": 2.38 * mm});
            skCircle(sketch, "E8.0.2.44", {"center": v(-546.1, -1136.65) * mm, "radius": 2.38 * mm});
            skCircle(sketch, "E8.0.2.45", {"center": v(-546.1, -1162.05) * mm, "radius": 2.38 * mm});
            skCircle(sketch, "E8.0.3.25", {"center": v(-520.7, -654.05) * mm, "radius": 2.38 * mm});
            skCircle(sketch, "E8.0.3.26", {"center": v(-520.7, -679.45) * mm, "radius": 2.38 * mm});
            skCircle(sketch, "E8.0.3.27", {"center": v(-520.7, -704.85) * mm, "radius": 2.38 * mm});
            skCircle(sketch, "E8.0.3.28", {"center": v(-520.7, -730.25) * mm, "radius": 2.38 * mm});
            skCircle(sketch, "E8.0.3.29", {"center": v(-520.7, -755.65) * mm, "radius": 2.38 * mm});
            skCircle(sketch, "E8.0.3.30", {"center": v(-520.7, -781.05) * mm, "radius": 2.38 * mm});
            skCircle(sketch, "E8.0.3.31", {"center": v(-520.7, -806.45) * mm, "radius": 2.38 * mm});
            skCircle(sketch, "E8.0.3.32", {"center": v(-520.7, -831.85) * mm, "radius": 2.38 * mm});
            skCircle(sketch, "E8.0.3.33", {"center": v(-520.7, -857.25) * mm, "radius": 2.38 * mm});
            skCircle(sketch, "E8.0.3.34", {"center": v(-520.7, -882.65) * mm, "radius": 2.38 * mm});
            skCircle(sketch, "E8.0.3.35", {"center": v(-520.7, -908.05) * mm, "radius": 2.38 * mm});
            skCircle(sketch, "E8.0.3.36", {"center": v(-520.7, -933.45) * mm, "radius": 2.38 * mm});
            skCircle(sketch, "E8.0.3.37", {"center": v(-520.7, -958.85) * mm, "radius": 2.38 * mm});
            skCircle(sketch, "E8.0.3.38", {"center": v(-520.7, -984.25) * mm, "radius": 2.38 * mm});
            skCircle(sketch, "E8.0.3.39", {"center": v(-520.7, -1009.65) * mm, "radius": 2.38 * mm});
            skCircle(sketch, "E8.0.3.40", {"center": v(-520.7, -1035.05) * mm, "radius": 2.38 * mm});
            skCircle(sketch, "E8.0.3.41", {"center": v(-520.7, -1060.45) * mm, "radius": 2.38 * mm});
            skCircle(sketch, "E8.0.3.42", {"center": v(-520.7, -1085.85) * mm, "radius": 2.38 * mm});
            skCircle(sketch, "E8.0.3.43", {"center": v(-520.7, -1111.25) * mm, "radius": 2.38 * mm});
            skCircle(sketch, "E8.0.3.44", {"center": v(-520.7, -1136.65) * mm, "radius": 2.38 * mm});
            skCircle(sketch, "E8.0.3.45", {"center": v(-520.7, -1162.05) * mm, "radius": 2.38 * mm});
            skCircle(sketch, "E8.0.4.25", {"center": v(-495.3, -654.05) * mm, "radius": 2.38 * mm});
            skCircle(sketch, "E8.0.4.26", {"center": v(-495.3, -679.45) * mm, "radius": 2.38 * mm});
            skCircle(sketch, "E8.0.4.27", {"center": v(-495.3, -704.85) * mm, "radius": 2.38 * mm});
            skCircle(sketch, "E8.0.4.28", {"center": v(-495.3, -730.25) * mm, "radius": 2.38 * mm});
            skCircle(sketch, "E8.0.4.29", {"center": v(-495.3, -755.65) * mm, "radius": 2.38 * mm});
            skCircle(sketch, "E8.0.4.30", {"center": v(-495.3, -781.05) * mm, "radius": 2.38 * mm});
            skCircle(sketch, "E8.0.4.31", {"center": v(-495.3, -806.45) * mm, "radius": 2.38 * mm});
            skCircle(sketch, "E8.0.4.32", {"center": v(-495.3, -831.85) * mm, "radius": 2.38 * mm});
            skCircle(sketch, "E8.0.4.33", {"center": v(-495.3, -857.25) * mm, "radius": 2.38 * mm});
            skCircle(sketch, "E8.0.4.34", {"center": v(-495.3, -882.65) * mm, "radius": 2.38 * mm});
            skCircle(sketch, "E8.0.4.35", {"center": v(-495.3, -908.05) * mm, "radius": 2.38 * mm});
            skCircle(sketch, "E8.0.4.36", {"center": v(-495.3, -933.45) * mm, "radius": 2.38 * mm});
            skCircle(sketch, "E8.0.4.37", {"center": v(-495.3, -958.85) * mm, "radius": 2.38 * mm});
            skCircle(sketch, "E8.0.4.38", {"center": v(-495.3, -984.25) * mm, "radius": 2.38 * mm});
            skCircle(sketch, "E8.0.4.39", {"center": v(-495.3, -1009.65) * mm, "radius": 2.38 * mm});
            skCircle(sketch, "E8.0.4.40", {"center": v(-495.3, -1035.05) * mm, "radius": 2.38 * mm});
            skCircle(sketch, "E8.0.4.41", {"center": v(-495.3, -1060.45) * mm, "radius": 2.38 * mm});
            skCircle(sketch, "E8.0.4.42", {"center": v(-495.3, -1085.85) * mm, "radius": 2.38 * mm});
            skCircle(sketch, "E8.0.4.43", {"center": v(-495.3, -1111.25) * mm, "radius": 2.38 * mm});
            skCircle(sketch, "E8.0.4.44", {"center": v(-495.3, -1136.65) * mm, "radius": 2.38 * mm});
            skCircle(sketch, "E8.0.4.45", {"center": v(-495.3, -1162.05) * mm, "radius": 2.38 * mm});
            skCircle(sketch, "E8.0.5.25", {"center": v(-469.9, -654.05) * mm, "radius": 2.38 * mm});
            skCircle(sketch, "E8.0.5.26", {"center": v(-469.9, -679.45) * mm, "radius": 2.38 * mm});
            skCircle(sketch, "E8.0.5.27", {"center": v(-469.9, -704.85) * mm, "radius": 2.38 * mm});
            skCircle(sketch, "E8.0.5.28", {"center": v(-469.9, -730.25) * mm, "radius": 2.38 * mm});
            skCircle(sketch, "E8.0.5.29", {"center": v(-469.9, -755.65) * mm, "radius": 2.38 * mm});
            skCircle(sketch, "E8.0.5.30", {"center": v(-469.9, -781.05) * mm, "radius": 2.38 * mm});
            skCircle(sketch, "E8.0.5.31", {"center": v(-469.9, -806.45) * mm, "radius": 2.38 * mm});
            skCircle(sketch, "E8.0.5.32", {"center": v(-469.9, -831.85) * mm, "radius": 2.38 * mm});
            skCircle(sketch, "E8.0.5.33", {"center": v(-469.9, -857.25) * mm, "radius": 2.38 * mm});
            skCircle(sketch, "E8.0.5.34", {"center": v(-469.9, -882.65) * mm, "radius": 2.38 * mm});
            skCircle(sketch, "E8.0.5.35", {"center": v(-469.9, -908.05) * mm, "radius": 2.38 * mm});
            skCircle(sketch, "E8.0.5.36", {"center": v(-469.9, -933.45) * mm, "radius": 2.38 * mm});
            skCircle(sketch, "E8.0.5.37", {"center": v(-469.9, -958.85) * mm, "radius": 2.38 * mm});
            skCircle(sketch, "E8.0.5.38", {"center": v(-469.9, -984.25) * mm, "radius": 2.38 * mm});
            skCircle(sketch, "E8.0.5.39", {"center": v(-469.9, -1009.65) * mm, "radius": 2.38 * mm});
            skCircle(sketch, "E8.0.5.40", {"center": v(-469.9, -1035.05) * mm, "radius": 2.38 * mm});
            skCircle(sketch, "E8.0.5.41", {"center": v(-469.9, -1060.45) * mm, "radius": 2.38 * mm});
            skCircle(sketch, "E8.0.5.42", {"center": v(-469.9, -1085.85) * mm, "radius": 2.38 * mm});
            skCircle(sketch, "E8.0.5.43", {"center": v(-469.9, -1111.25) * mm, "radius": 2.38 * mm});
            skCircle(sketch, "E8.0.5.44", {"center": v(-469.9, -1136.65) * mm, "radius": 2.38 * mm});
            skCircle(sketch, "E8.0.5.45", {"center": v(-469.9, -1162.05) * mm, "radius": 2.38 * mm});
            skCircle(sketch, "E8.0.6.25", {"center": v(-444.5, -654.05) * mm, "radius": 2.38 * mm});
            skCircle(sketch, "E8.0.6.26", {"center": v(-444.5, -679.45) * mm, "radius": 2.38 * mm});
            skCircle(sketch, "E8.0.6.27", {"center": v(-444.5, -704.85) * mm, "radius": 2.38 * mm});
            skCircle(sketch, "E8.0.6.28", {"center": v(-444.5, -730.25) * mm, "radius": 2.38 * mm});
            skCircle(sketch, "E8.0.6.29", {"center": v(-444.5, -755.65) * mm, "radius": 2.38 * mm});
            skCircle(sketch, "E8.0.6.30", {"center": v(-444.5, -781.05) * mm, "radius": 2.38 * mm});
            skCircle(sketch, "E8.0.6.31", {"center": v(-444.5, -806.45) * mm, "radius": 2.38 * mm});
            skCircle(sketch, "E8.0.6.32", {"center": v(-444.5, -831.85) * mm, "radius": 2.38 * mm});
            skCircle(sketch, "E8.0.6.33", {"center": v(-444.5, -857.25) * mm, "radius": 2.38 * mm});
            skCircle(sketch, "E8.0.6.34", {"center": v(-444.5, -882.65) * mm, "radius": 2.38 * mm});
            skCircle(sketch, "E8.0.6.35", {"center": v(-444.5, -908.05) * mm, "radius": 2.38 * mm});
            skCircle(sketch, "E8.0.6.36", {"center": v(-444.5, -933.45) * mm, "radius": 2.38 * mm});
            skCircle(sketch, "E8.0.6.37", {"center": v(-444.5, -958.85) * mm, "radius": 2.38 * mm});
            skCircle(sketch, "E8.0.6.38", {"center": v(-444.5, -984.25) * mm, "radius": 2.38 * mm});
            skCircle(sketch, "E8.0.6.39", {"center": v(-444.5, -1009.65) * mm, "radius": 2.38 * mm});
            skCircle(sketch, "E8.0.6.40", {"center": v(-444.5, -1035.05) * mm, "radius": 2.38 * mm});
            skCircle(sketch, "E8.0.6.41", {"center": v(-444.5, -1060.45) * mm, "radius": 2.38 * mm});
            skCircle(sketch, "E8.0.6.42", {"center": v(-444.5, -1085.85) * mm, "radius": 2.38 * mm});
            skCircle(sketch, "E8.0.6.43", {"center": v(-444.5, -1111.25) * mm, "radius": 2.38 * mm});
            skCircle(sketch, "E8.0.6.44", {"center": v(-444.5, -1136.65) * mm, "radius": 2.38 * mm});
            skCircle(sketch, "E8.0.6.45", {"center": v(-444.5, -1162.05) * mm, "radius": 2.38 * mm});
            skCircle(sketch, "E8.0.7.25", {"center": v(-419.1, -654.05) * mm, "radius": 2.38 * mm});
            skCircle(sketch, "E8.0.7.26", {"center": v(-419.1, -679.45) * mm, "radius": 2.38 * mm});
            skCircle(sketch, "E8.0.7.27", {"center": v(-419.1, -704.85) * mm, "radius": 2.38 * mm});
            skCircle(sketch, "E8.0.7.28", {"center": v(-419.1, -730.25) * mm, "radius": 2.38 * mm});
            skCircle(sketch, "E8.0.7.29", {"center": v(-419.1, -755.65) * mm, "radius": 2.38 * mm});
            skCircle(sketch, "E8.0.7.30", {"center": v(-419.1, -781.05) * mm, "radius": 2.38 * mm});
            skCircle(sketch, "E8.0.7.31", {"center": v(-419.1, -806.45) * mm, "radius": 2.38 * mm});
            skCircle(sketch, "E8.0.7.32", {"center": v(-419.1, -831.85) * mm, "radius": 2.38 * mm});
            skCircle(sketch, "E8.0.7.33", {"center": v(-419.1, -857.25) * mm, "radius": 2.38 * mm});
            skCircle(sketch, "E8.0.7.34", {"center": v(-419.1, -882.65) * mm, "radius": 2.38 * mm});
            skCircle(sketch, "E8.0.7.35", {"center": v(-419.1, -908.05) * mm, "radius": 2.38 * mm});
            skCircle(sketch, "E8.0.7.36", {"center": v(-419.1, -933.45) * mm, "radius": 2.38 * mm});
            skCircle(sketch, "E8.0.7.37", {"center": v(-419.1, -958.85) * mm, "radius": 2.38 * mm});
            skCircle(sketch, "E8.0.7.38", {"center": v(-419.1, -984.25) * mm, "radius": 2.38 * mm});
            skCircle(sketch, "E8.0.7.39", {"center": v(-419.1, -1009.65) * mm, "radius": 2.38 * mm});
            skCircle(sketch, "E8.0.7.40", {"center": v(-419.1, -1035.05) * mm, "radius": 2.38 * mm});
            skCircle(sketch, "E8.0.7.41", {"center": v(-419.1, -1060.45) * mm, "radius": 2.38 * mm});
            skCircle(sketch, "E8.0.7.42", {"center": v(-419.1, -1085.85) * mm, "radius": 2.38 * mm});
            skCircle(sketch, "E8.0.7.43", {"center": v(-419.1, -1111.25) * mm, "radius": 2.38 * mm});
            skCircle(sketch, "E8.0.7.44", {"center": v(-419.1, -1136.65) * mm, "radius": 2.38 * mm});
            skCircle(sketch, "E8.0.7.45", {"center": v(-419.1, -1162.05) * mm, "radius": 2.38 * mm});
            skCircle(sketch, "E8.0.8.25", {"center": v(-393.7, -654.05) * mm, "radius": 2.38 * mm});
            skCircle(sketch, "E8.0.8.26", {"center": v(-393.7, -679.45) * mm, "radius": 2.38 * mm});
            skCircle(sketch, "E8.0.8.27", {"center": v(-393.7, -704.85) * mm, "radius": 2.38 * mm});
            skCircle(sketch, "E8.0.8.28", {"center": v(-393.7, -730.25) * mm, "radius": 2.38 * mm});
            skCircle(sketch, "E8.0.8.29", {"center": v(-393.7, -755.65) * mm, "radius": 2.38 * mm});
            skCircle(sketch, "E8.0.8.30", {"center": v(-393.7, -781.05) * mm, "radius": 2.38 * mm});
            skCircle(sketch, "E8.0.8.31", {"center": v(-393.7, -806.45) * mm, "radius": 2.38 * mm});
            skCircle(sketch, "E8.0.8.32", {"center": v(-393.7, -831.85) * mm, "radius": 2.38 * mm});
            skCircle(sketch, "E8.0.8.33", {"center": v(-393.7, -857.25) * mm, "radius": 2.38 * mm});
            skCircle(sketch, "E8.0.8.34", {"center": v(-393.7, -882.65) * mm, "radius": 2.38 * mm});
            skCircle(sketch, "E8.0.8.35", {"center": v(-393.7, -908.05) * mm, "radius": 2.38 * mm});
            skCircle(sketch, "E8.0.8.36", {"center": v(-393.7, -933.45) * mm, "radius": 2.38 * mm});
            skCircle(sketch, "E8.0.8.37", {"center": v(-393.7, -958.85) * mm, "radius": 2.38 * mm});
            skCircle(sketch, "E8.0.8.38", {"center": v(-393.7, -984.25) * mm, "radius": 2.38 * mm});
            skCircle(sketch, "E8.0.8.39", {"center": v(-393.7, -1009.65) * mm, "radius": 2.38 * mm});
            skCircle(sketch, "E8.0.8.40", {"center": v(-393.7, -1035.05) * mm, "radius": 2.38 * mm});
            skCircle(sketch, "E8.0.8.41", {"center": v(-393.7, -1060.45) * mm, "radius": 2.38 * mm});
            skCircle(sketch, "E8.0.8.42", {"center": v(-393.7, -1085.85) * mm, "radius": 2.38 * mm});
            skCircle(sketch, "E8.0.8.43", {"center": v(-393.7, -1111.25) * mm, "radius": 2.38 * mm});
            skCircle(sketch, "E8.0.8.44", {"center": v(-393.7, -1136.65) * mm, "radius": 2.38 * mm});
            skCircle(sketch, "E8.0.8.45", {"center": v(-393.7, -1162.05) * mm, "radius": 2.38 * mm});
            skCircle(sketch, "E8.0.9.25", {"center": v(-368.3, -654.05) * mm, "radius": 2.38 * mm});
            skCircle(sketch, "E8.0.9.26", {"center": v(-368.3, -679.45) * mm, "radius": 2.38 * mm});
            skCircle(sketch, "E8.0.9.27", {"center": v(-368.3, -704.85) * mm, "radius": 2.38 * mm});
            skCircle(sketch, "E8.0.9.28", {"center": v(-368.3, -730.25) * mm, "radius": 2.38 * mm});
            skCircle(sketch, "E8.0.9.29", {"center": v(-368.3, -755.65) * mm, "radius": 2.38 * mm});
            skCircle(sketch, "E8.0.9.30", {"center": v(-368.3, -781.05) * mm, "radius": 2.38 * mm});
            skCircle(sketch, "E8.0.9.31", {"center": v(-368.3, -806.45) * mm, "radius": 2.38 * mm});
            skCircle(sketch, "E8.0.9.32", {"center": v(-368.3, -831.85) * mm, "radius": 2.38 * mm});
            skCircle(sketch, "E8.0.9.33", {"center": v(-368.3, -857.25) * mm, "radius": 2.38 * mm});
            skCircle(sketch, "E8.0.9.34", {"center": v(-368.3, -882.65) * mm, "radius": 2.38 * mm});
            skCircle(sketch, "E8.0.9.35", {"center": v(-368.3, -908.05) * mm, "radius": 2.38 * mm});
            skCircle(sketch, "E8.0.9.36", {"center": v(-368.3, -933.45) * mm, "radius": 2.38 * mm});
            skCircle(sketch, "E8.0.9.37", {"center": v(-368.3, -958.85) * mm, "radius": 2.38 * mm});
            skCircle(sketch, "E8.0.9.38", {"center": v(-368.3, -984.25) * mm, "radius": 2.38 * mm});
            skCircle(sketch, "E8.0.9.39", {"center": v(-368.3, -1009.65) * mm, "radius": 2.38 * mm});
            skCircle(sketch, "E8.0.9.40", {"center": v(-368.3, -1035.05) * mm, "radius": 2.38 * mm});
            skCircle(sketch, "E8.0.9.41", {"center": v(-368.3, -1060.45) * mm, "radius": 2.38 * mm});
            skCircle(sketch, "E8.0.9.42", {"center": v(-368.3, -1085.85) * mm, "radius": 2.38 * mm});
            skCircle(sketch, "E8.0.9.43", {"center": v(-368.3, -1111.25) * mm, "radius": 2.38 * mm});
            skCircle(sketch, "E8.0.9.44", {"center": v(-368.3, -1136.65) * mm, "radius": 2.38 * mm});
            skCircle(sketch, "E8.0.9.45", {"center": v(-368.3, -1162.05) * mm, "radius": 2.38 * mm});
            skCircle(sketch, "E8.0.10.25", {"center": v(-342.9, -654.05) * mm, "radius": 2.38 * mm});
            skCircle(sketch, "E8.0.10.26", {"center": v(-342.9, -679.45) * mm, "radius": 2.38 * mm});
            skCircle(sketch, "E8.0.10.27", {"center": v(-342.9, -704.85) * mm, "radius": 2.38 * mm});
            skCircle(sketch, "E8.0.10.28", {"center": v(-342.9, -730.25) * mm, "radius": 2.38 * mm});
            skCircle(sketch, "E8.0.10.29", {"center": v(-342.9, -755.65) * mm, "radius": 2.38 * mm});
            skCircle(sketch, "E8.0.10.30", {"center": v(-342.9, -781.05) * mm, "radius": 2.38 * mm});
            skCircle(sketch, "E8.0.10.31", {"center": v(-342.9, -806.45) * mm, "radius": 2.38 * mm});
            skCircle(sketch, "E8.0.10.32", {"center": v(-342.9, -831.85) * mm, "radius": 2.38 * mm});
            skCircle(sketch, "E8.0.10.33", {"center": v(-342.9, -857.25) * mm, "radius": 2.38 * mm});
            skCircle(sketch, "E8.0.10.34", {"center": v(-342.9, -882.65) * mm, "radius": 2.38 * mm});
            skCircle(sketch, "E8.0.10.35", {"center": v(-342.9, -908.05) * mm, "radius": 2.38 * mm});
            skCircle(sketch, "E8.0.10.36", {"center": v(-342.9, -933.45) * mm, "radius": 2.38 * mm});
            skCircle(sketch, "E8.0.10.37", {"center": v(-342.9, -958.85) * mm, "radius": 2.38 * mm});
            skCircle(sketch, "E8.0.10.38", {"center": v(-342.9, -984.25) * mm, "radius": 2.38 * mm});
            skCircle(sketch, "E8.0.10.39", {"center": v(-342.9, -1009.65) * mm, "radius": 2.38 * mm});
            skCircle(sketch, "E8.0.10.40", {"center": v(-342.9, -1035.05) * mm, "radius": 2.38 * mm});
            skCircle(sketch, "E8.0.10.41", {"center": v(-342.9, -1060.45) * mm, "radius": 2.38 * mm});
            skCircle(sketch, "E8.0.10.42", {"center": v(-342.9, -1085.85) * mm, "radius": 2.38 * mm});
            skCircle(sketch, "E8.0.10.43", {"center": v(-342.9, -1111.25) * mm, "radius": 2.38 * mm});
            skCircle(sketch, "E8.0.10.44", {"center": v(-342.9, -1136.65) * mm, "radius": 2.38 * mm});
            skCircle(sketch, "E8.0.10.45", {"center": v(-342.9, -1162.05) * mm, "radius": 2.38 * mm});
            skCircle(sketch, "E8.0.11.25", {"center": v(-317.5, -654.05) * mm, "radius": 2.38 * mm});
            skCircle(sketch, "E8.0.11.26", {"center": v(-317.5, -679.45) * mm, "radius": 2.38 * mm});
            skCircle(sketch, "E8.0.11.27", {"center": v(-317.5, -704.85) * mm, "radius": 2.38 * mm});
            skCircle(sketch, "E8.0.11.28", {"center": v(-317.5, -730.25) * mm, "radius": 2.38 * mm});
            skCircle(sketch, "E8.0.11.29", {"center": v(-317.5, -755.65) * mm, "radius": 2.38 * mm});
            skCircle(sketch, "E8.0.11.30", {"center": v(-317.5, -781.05) * mm, "radius": 2.38 * mm});
            skCircle(sketch, "E8.0.11.31", {"center": v(-317.5, -806.45) * mm, "radius": 2.38 * mm});
            skCircle(sketch, "E8.0.11.32", {"center": v(-317.5, -831.85) * mm, "radius": 2.38 * mm});
            skCircle(sketch, "E8.0.11.33", {"center": v(-317.5, -857.25) * mm, "radius": 2.38 * mm});
            skCircle(sketch, "E8.0.11.34", {"center": v(-317.5, -882.65) * mm, "radius": 2.38 * mm});
            skCircle(sketch, "E8.0.11.35", {"center": v(-317.5, -908.05) * mm, "radius": 2.38 * mm});
            skCircle(sketch, "E8.0.11.36", {"center": v(-317.5, -933.45) * mm, "radius": 2.38 * mm});
            skCircle(sketch, "E8.0.11.37", {"center": v(-317.5, -958.85) * mm, "radius": 2.38 * mm});
            skCircle(sketch, "E8.0.11.38", {"center": v(-317.5, -984.25) * mm, "radius": 2.38 * mm});
            skCircle(sketch, "E8.0.11.39", {"center": v(-317.5, -1009.65) * mm, "radius": 2.38 * mm});
            skCircle(sketch, "E8.0.11.40", {"center": v(-317.5, -1035.05) * mm, "radius": 2.38 * mm});
            skCircle(sketch, "E8.0.11.41", {"center": v(-317.5, -1060.45) * mm, "radius": 2.38 * mm});
            skCircle(sketch, "E8.0.11.42", {"center": v(-317.5, -1085.85) * mm, "radius": 2.38 * mm});
            skCircle(sketch, "E8.0.11.43", {"center": v(-317.5, -1111.25) * mm, "radius": 2.38 * mm});
            skCircle(sketch, "E8.0.11.44", {"center": v(-317.5, -1136.65) * mm, "radius": 2.38 * mm});
            skCircle(sketch, "E8.0.11.45", {"center": v(-317.5, -1162.05) * mm, "radius": 2.38 * mm});
            skCircle(sketch, "E8.0.12.25", {"center": v(-292.1, -654.05) * mm, "radius": 2.38 * mm});
            skCircle(sketch, "E8.0.12.26", {"center": v(-292.1, -679.45) * mm, "radius": 2.38 * mm});
            skCircle(sketch, "E8.0.12.27", {"center": v(-292.1, -704.85) * mm, "radius": 2.38 * mm});
            skCircle(sketch, "E8.0.12.28", {"center": v(-292.1, -730.25) * mm, "radius": 2.38 * mm});
            skCircle(sketch, "E8.0.12.29", {"center": v(-292.1, -755.65) * mm, "radius": 2.38 * mm});
            skCircle(sketch, "E8.0.12.30", {"center": v(-292.1, -781.05) * mm, "radius": 2.38 * mm});
            skCircle(sketch, "E8.0.12.31", {"center": v(-292.1, -806.45) * mm, "radius": 2.38 * mm});
            skCircle(sketch, "E8.0.12.32", {"center": v(-292.1, -831.85) * mm, "radius": 2.38 * mm});
            skCircle(sketch, "E8.0.12.33", {"center": v(-292.1, -857.25) * mm, "radius": 2.38 * mm});
            skCircle(sketch, "E8.0.12.34", {"center": v(-292.1, -882.65) * mm, "radius": 2.38 * mm});
            skCircle(sketch, "E8.0.12.35", {"center": v(-292.1, -908.05) * mm, "radius": 2.38 * mm});
            skCircle(sketch, "E8.0.12.36", {"center": v(-292.1, -933.45) * mm, "radius": 2.38 * mm});
            skCircle(sketch, "E8.0.12.37", {"center": v(-292.1, -958.85) * mm, "radius": 2.38 * mm});
            skCircle(sketch, "E8.0.12.38", {"center": v(-292.1, -984.25) * mm, "radius": 2.38 * mm});
            skCircle(sketch, "E8.0.12.39", {"center": v(-292.1, -1009.65) * mm, "radius": 2.38 * mm});
            skCircle(sketch, "E8.0.12.40", {"center": v(-292.1, -1035.05) * mm, "radius": 2.38 * mm});
            skCircle(sketch, "E8.0.12.41", {"center": v(-292.1, -1060.45) * mm, "radius": 2.38 * mm});
            skCircle(sketch, "E8.0.12.42", {"center": v(-292.1, -1085.85) * mm, "radius": 2.38 * mm});
            skCircle(sketch, "E8.0.12.43", {"center": v(-292.1, -1111.25) * mm, "radius": 2.38 * mm});
            skCircle(sketch, "E8.0.12.44", {"center": v(-292.1, -1136.65) * mm, "radius": 2.38 * mm});
            skCircle(sketch, "E8.0.12.45", {"center": v(-292.1, -1162.05) * mm, "radius": 2.38 * mm});
            skCircle(sketch, "E8.0.13.25", {"center": v(-266.7, -654.05) * mm, "radius": 2.38 * mm});
            skCircle(sketch, "E8.0.13.26", {"center": v(-266.7, -679.45) * mm, "radius": 2.38 * mm});
            skCircle(sketch, "E8.0.13.27", {"center": v(-266.7, -704.85) * mm, "radius": 2.38 * mm});
            skCircle(sketch, "E8.0.13.28", {"center": v(-266.7, -730.25) * mm, "radius": 2.38 * mm});
            skCircle(sketch, "E8.0.13.29", {"center": v(-266.7, -755.65) * mm, "radius": 2.38 * mm});
            skCircle(sketch, "E8.0.13.30", {"center": v(-266.7, -781.05) * mm, "radius": 2.38 * mm});
            skCircle(sketch, "E8.0.13.31", {"center": v(-266.7, -806.45) * mm, "radius": 2.38 * mm});
            skCircle(sketch, "E8.0.13.32", {"center": v(-266.7, -831.85) * mm, "radius": 2.38 * mm});
            skCircle(sketch, "E8.0.13.33", {"center": v(-266.7, -857.25) * mm, "radius": 2.38 * mm});
            skCircle(sketch, "E8.0.13.34", {"center": v(-266.7, -882.65) * mm, "radius": 2.38 * mm});
            skCircle(sketch, "E8.0.13.35", {"center": v(-266.7, -908.05) * mm, "radius": 2.38 * mm});
            skCircle(sketch, "E8.0.13.36", {"center": v(-266.7, -933.45) * mm, "radius": 2.38 * mm});
            skCircle(sketch, "E8.0.13.37", {"center": v(-266.7, -958.85) * mm, "radius": 2.38 * mm});
            skCircle(sketch, "E8.0.13.38", {"center": v(-266.7, -984.25) * mm, "radius": 2.38 * mm});
            skCircle(sketch, "E8.0.13.39", {"center": v(-266.7, -1009.65) * mm, "radius": 2.38 * mm});
            skCircle(sketch, "E8.0.13.40", {"center": v(-266.7, -1035.05) * mm, "radius": 2.38 * mm});
            skCircle(sketch, "E8.0.13.41", {"center": v(-266.7, -1060.45) * mm, "radius": 2.38 * mm});
            skCircle(sketch, "E8.0.13.42", {"center": v(-266.7, -1085.85) * mm, "radius": 2.38 * mm});
            skCircle(sketch, "E8.0.13.43", {"center": v(-266.7, -1111.25) * mm, "radius": 2.38 * mm});
            skCircle(sketch, "E8.0.13.44", {"center": v(-266.7, -1136.65) * mm, "radius": 2.38 * mm});
            skCircle(sketch, "E8.0.13.45", {"center": v(-266.7, -1162.05) * mm, "radius": 2.38 * mm});
            skCircle(sketch, "E8.0.14.25", {"center": v(-241.3, -654.05) * mm, "radius": 2.38 * mm});
            skCircle(sketch, "E8.0.14.26", {"center": v(-241.3, -679.45) * mm, "radius": 2.38 * mm});
            skCircle(sketch, "E8.0.14.27", {"center": v(-241.3, -704.85) * mm, "radius": 2.38 * mm});
            skCircle(sketch, "E8.0.14.28", {"center": v(-241.3, -730.25) * mm, "radius": 2.38 * mm});
            skCircle(sketch, "E8.0.14.29", {"center": v(-241.3, -755.65) * mm, "radius": 2.38 * mm});
            skCircle(sketch, "E8.0.14.30", {"center": v(-241.3, -781.05) * mm, "radius": 2.38 * mm});
            skCircle(sketch, "E8.0.14.31", {"center": v(-241.3, -806.45) * mm, "radius": 2.38 * mm});
            skCircle(sketch, "E8.0.14.32", {"center": v(-241.3, -831.85) * mm, "radius": 2.38 * mm});
            skCircle(sketch, "E8.0.14.33", {"center": v(-241.3, -857.25) * mm, "radius": 2.38 * mm});
            skCircle(sketch, "E8.0.14.34", {"center": v(-241.3, -882.65) * mm, "radius": 2.38 * mm});
            skCircle(sketch, "E8.0.14.35", {"center": v(-241.3, -908.05) * mm, "radius": 2.38 * mm});
            skCircle(sketch, "E8.0.14.36", {"center": v(-241.3, -933.45) * mm, "radius": 2.38 * mm});
            skCircle(sketch, "E8.0.14.37", {"center": v(-241.3, -958.85) * mm, "radius": 2.38 * mm});
            skCircle(sketch, "E8.0.14.38", {"center": v(-241.3, -984.25) * mm, "radius": 2.38 * mm});
            skCircle(sketch, "E8.0.14.39", {"center": v(-241.3, -1009.65) * mm, "radius": 2.38 * mm});
            skCircle(sketch, "E8.0.14.40", {"center": v(-241.3, -1035.05) * mm, "radius": 2.38 * mm});
            skCircle(sketch, "E8.0.14.41", {"center": v(-241.3, -1060.45) * mm, "radius": 2.38 * mm});
            skCircle(sketch, "E8.0.14.42", {"center": v(-241.3, -1085.85) * mm, "radius": 2.38 * mm});
            skCircle(sketch, "E8.0.14.43", {"center": v(-241.3, -1111.25) * mm, "radius": 2.38 * mm});
            skCircle(sketch, "E8.0.14.44", {"center": v(-241.3, -1136.65) * mm, "radius": 2.38 * mm});
            skCircle(sketch, "E8.0.14.45", {"center": v(-241.3, -1162.05) * mm, "radius": 2.38 * mm});
            skCircle(sketch, "E8.0.15.25", {"center": v(-215.9, -654.05) * mm, "radius": 2.38 * mm});
            skCircle(sketch, "E8.0.15.26", {"center": v(-215.9, -679.45) * mm, "radius": 2.38 * mm});
            skCircle(sketch, "E8.0.15.27", {"center": v(-215.9, -704.85) * mm, "radius": 2.38 * mm});
            skCircle(sketch, "E8.0.15.28", {"center": v(-215.9, -730.25) * mm, "radius": 2.38 * mm});
            skCircle(sketch, "E8.0.15.29", {"center": v(-215.9, -755.65) * mm, "radius": 2.38 * mm});
            skCircle(sketch, "E8.0.15.30", {"center": v(-215.9, -781.05) * mm, "radius": 2.38 * mm});
            skCircle(sketch, "E8.0.15.31", {"center": v(-215.9, -806.45) * mm, "radius": 2.38 * mm});
            skCircle(sketch, "E8.0.15.32", {"center": v(-215.9, -831.85) * mm, "radius": 2.38 * mm});
            skCircle(sketch, "E8.0.15.33", {"center": v(-215.9, -857.25) * mm, "radius": 2.38 * mm});
            skCircle(sketch, "E8.0.15.34", {"center": v(-215.9, -882.65) * mm, "radius": 2.38 * mm});
            skCircle(sketch, "E8.0.15.35", {"center": v(-215.9, -908.05) * mm, "radius": 2.38 * mm});
            skCircle(sketch, "E8.0.15.36", {"center": v(-215.9, -933.45) * mm, "radius": 2.38 * mm});
            skCircle(sketch, "E8.0.15.37", {"center": v(-215.9, -958.85) * mm, "radius": 2.38 * mm});
            skCircle(sketch, "E8.0.15.38", {"center": v(-215.9, -984.25) * mm, "radius": 2.38 * mm});
            skCircle(sketch, "E8.0.15.39", {"center": v(-215.9, -1009.65) * mm, "radius": 2.38 * mm});
            skCircle(sketch, "E8.0.15.40", {"center": v(-215.9, -1035.05) * mm, "radius": 2.38 * mm});
            skCircle(sketch, "E8.0.15.41", {"center": v(-215.9, -1060.45) * mm, "radius": 2.38 * mm});
            skCircle(sketch, "E8.0.15.42", {"center": v(-215.9, -1085.85) * mm, "radius": 2.38 * mm});
            skCircle(sketch, "E8.0.15.43", {"center": v(-215.9, -1111.25) * mm, "radius": 2.38 * mm});
            skCircle(sketch, "E8.0.15.44", {"center": v(-215.9, -1136.65) * mm, "radius": 2.38 * mm});
            skCircle(sketch, "E8.0.15.45", {"center": v(-215.9, -1162.05) * mm, "radius": 2.38 * mm});
            skCircle(sketch, "E8.0.16.25", {"center": v(-190.5, -654.05) * mm, "radius": 2.38 * mm});
            skCircle(sketch, "E8.0.16.26", {"center": v(-190.5, -679.45) * mm, "radius": 2.38 * mm});
            skCircle(sketch, "E8.0.16.27", {"center": v(-190.5, -704.85) * mm, "radius": 2.38 * mm});
            skCircle(sketch, "E8.0.16.28", {"center": v(-190.5, -730.25) * mm, "radius": 2.38 * mm});
            skCircle(sketch, "E8.0.16.29", {"center": v(-190.5, -755.65) * mm, "radius": 2.38 * mm});
            skCircle(sketch, "E8.0.16.30", {"center": v(-190.5, -781.05) * mm, "radius": 2.38 * mm});
            skCircle(sketch, "E8.0.16.31", {"center": v(-190.5, -806.45) * mm, "radius": 2.38 * mm});
            skCircle(sketch, "E8.0.16.32", {"center": v(-190.5, -831.85) * mm, "radius": 2.38 * mm});
            skCircle(sketch, "E8.0.16.33", {"center": v(-190.5, -857.25) * mm, "radius": 2.38 * mm});
            skCircle(sketch, "E8.0.16.34", {"center": v(-190.5, -882.65) * mm, "radius": 2.38 * mm});
            skCircle(sketch, "E8.0.16.35", {"center": v(-190.5, -908.05) * mm, "radius": 2.38 * mm});
            skCircle(sketch, "E8.0.16.36", {"center": v(-190.5, -933.45) * mm, "radius": 2.38 * mm});
            skCircle(sketch, "E8.0.16.37", {"center": v(-190.5, -958.85) * mm, "radius": 2.38 * mm});
            skCircle(sketch, "E8.0.16.38", {"center": v(-190.5, -984.25) * mm, "radius": 2.38 * mm});
            skCircle(sketch, "E8.0.16.39", {"center": v(-190.5, -1009.65) * mm, "radius": 2.38 * mm});
            skCircle(sketch, "E8.0.16.40", {"center": v(-190.5, -1035.05) * mm, "radius": 2.38 * mm});
            skCircle(sketch, "E8.0.16.41", {"center": v(-190.5, -1060.45) * mm, "radius": 2.38 * mm});
            skCircle(sketch, "E8.0.16.42", {"center": v(-190.5, -1085.85) * mm, "radius": 2.38 * mm});
            skCircle(sketch, "E8.0.16.43", {"center": v(-190.5, -1111.25) * mm, "radius": 2.38 * mm});
            skCircle(sketch, "E8.0.16.44", {"center": v(-190.5, -1136.65) * mm, "radius": 2.38 * mm});
            skCircle(sketch, "E8.0.16.45", {"center": v(-190.5, -1162.05) * mm, "radius": 2.38 * mm});
            skCircle(sketch, "E8.0.17.25", {"center": v(-165.1, -654.05) * mm, "radius": 2.38 * mm});
            skCircle(sketch, "E8.0.17.26", {"center": v(-165.1, -679.45) * mm, "radius": 2.38 * mm});
            skCircle(sketch, "E8.0.17.27", {"center": v(-165.1, -704.85) * mm, "radius": 2.38 * mm});
            skCircle(sketch, "E8.0.17.28", {"center": v(-165.1, -730.25) * mm, "radius": 2.38 * mm});
            skCircle(sketch, "E8.0.17.29", {"center": v(-165.1, -755.65) * mm, "radius": 2.38 * mm});
            skCircle(sketch, "E8.0.17.30", {"center": v(-165.1, -781.05) * mm, "radius": 2.38 * mm});
            skCircle(sketch, "E8.0.17.31", {"center": v(-165.1, -806.45) * mm, "radius": 2.38 * mm});
            skCircle(sketch, "E8.0.17.32", {"center": v(-165.1, -831.85) * mm, "radius": 2.38 * mm});
            skCircle(sketch, "E8.0.17.33", {"center": v(-165.1, -857.25) * mm, "radius": 2.38 * mm});
            skCircle(sketch, "E8.0.17.34", {"center": v(-165.1, -882.65) * mm, "radius": 2.38 * mm});
            skCircle(sketch, "E8.0.17.35", {"center": v(-165.1, -908.05) * mm, "radius": 2.38 * mm});
            skCircle(sketch, "E8.0.17.36", {"center": v(-165.1, -933.45) * mm, "radius": 2.38 * mm});
            skCircle(sketch, "E8.0.17.37", {"center": v(-165.1, -958.85) * mm, "radius": 2.38 * mm});
            skCircle(sketch, "E8.0.17.38", {"center": v(-165.1, -984.25) * mm, "radius": 2.38 * mm});
            skCircle(sketch, "E8.0.17.39", {"center": v(-165.1, -1009.65) * mm, "radius": 2.38 * mm});
            skCircle(sketch, "E8.0.17.40", {"center": v(-165.1, -1035.05) * mm, "radius": 2.38 * mm});
            skCircle(sketch, "E8.0.17.41", {"center": v(-165.1, -1060.45) * mm, "radius": 2.38 * mm});
            skCircle(sketch, "E8.0.17.42", {"center": v(-165.1, -1085.85) * mm, "radius": 2.38 * mm});
            skCircle(sketch, "E8.0.17.43", {"center": v(-165.1, -1111.25) * mm, "radius": 2.38 * mm});
            skCircle(sketch, "E8.0.17.44", {"center": v(-165.1, -1136.65) * mm, "radius": 2.38 * mm});
            skCircle(sketch, "E8.0.17.45", {"center": v(-165.1, -1162.05) * mm, "radius": 2.38 * mm});
            skCircle(sketch, "E8.0.18.25", {"center": v(-139.7, -654.05) * mm, "radius": 2.38 * mm});
            skCircle(sketch, "E8.0.18.26", {"center": v(-139.7, -679.45) * mm, "radius": 2.38 * mm});
            skCircle(sketch, "E8.0.18.27", {"center": v(-139.7, -704.85) * mm, "radius": 2.38 * mm});
            skCircle(sketch, "E8.0.18.28", {"center": v(-139.7, -730.25) * mm, "radius": 2.38 * mm});
            skCircle(sketch, "E8.0.18.29", {"center": v(-139.7, -755.65) * mm, "radius": 2.38 * mm});
            skCircle(sketch, "E8.0.18.30", {"center": v(-139.7, -781.05) * mm, "radius": 2.38 * mm});
            skCircle(sketch, "E8.0.18.31", {"center": v(-139.7, -806.45) * mm, "radius": 2.38 * mm});
            skCircle(sketch, "E8.0.18.32", {"center": v(-139.7, -831.85) * mm, "radius": 2.38 * mm});
            skCircle(sketch, "E8.0.18.33", {"center": v(-139.7, -857.25) * mm, "radius": 2.38 * mm});
            skCircle(sketch, "E8.0.18.34", {"center": v(-139.7, -882.65) * mm, "radius": 2.38 * mm});
            skCircle(sketch, "E8.0.18.35", {"center": v(-139.7, -908.05) * mm, "radius": 2.38 * mm});
            skCircle(sketch, "E8.0.18.36", {"center": v(-139.7, -933.45) * mm, "radius": 2.38 * mm});
            skCircle(sketch, "E8.0.18.37", {"center": v(-139.7, -958.85) * mm, "radius": 2.38 * mm});
            skCircle(sketch, "E8.0.18.38", {"center": v(-139.7, -984.25) * mm, "radius": 2.38 * mm});
            skCircle(sketch, "E8.0.18.39", {"center": v(-139.7, -1009.65) * mm, "radius": 2.38 * mm});
            skCircle(sketch, "E8.0.18.40", {"center": v(-139.7, -1035.05) * mm, "radius": 2.38 * mm});
            skCircle(sketch, "E8.0.18.41", {"center": v(-139.7, -1060.45) * mm, "radius": 2.38 * mm});
            skCircle(sketch, "E8.0.18.42", {"center": v(-139.7, -1085.85) * mm, "radius": 2.38 * mm});
            skCircle(sketch, "E8.0.18.43", {"center": v(-139.7, -1111.25) * mm, "radius": 2.38 * mm});
            skCircle(sketch, "E8.0.18.44", {"center": v(-139.7, -1136.65) * mm, "radius": 2.38 * mm});
            skCircle(sketch, "E8.0.18.45", {"center": v(-139.7, -1162.05) * mm, "radius": 2.38 * mm});
            skCircle(sketch, "E8.0.19.25", {"center": v(-114.3, -654.05) * mm, "radius": 2.38 * mm});
            skCircle(sketch, "E8.0.19.26", {"center": v(-114.3, -679.45) * mm, "radius": 2.38 * mm});
            skCircle(sketch, "E8.0.19.27", {"center": v(-114.3, -704.85) * mm, "radius": 2.38 * mm});
            skCircle(sketch, "E8.0.19.28", {"center": v(-114.3, -730.25) * mm, "radius": 2.38 * mm});
            skCircle(sketch, "E8.0.19.29", {"center": v(-114.3, -755.65) * mm, "radius": 2.38 * mm});
            skCircle(sketch, "E8.0.19.30", {"center": v(-114.3, -781.05) * mm, "radius": 2.38 * mm});
            skCircle(sketch, "E8.0.19.31", {"center": v(-114.3, -806.45) * mm, "radius": 2.38 * mm});
            skCircle(sketch, "E8.0.19.32", {"center": v(-114.3, -831.85) * mm, "radius": 2.38 * mm});
            skCircle(sketch, "E8.0.19.33", {"center": v(-114.3, -857.25) * mm, "radius": 2.38 * mm});
            skCircle(sketch, "E8.0.19.34", {"center": v(-114.3, -882.65) * mm, "radius": 2.38 * mm});
            skCircle(sketch, "E8.0.19.35", {"center": v(-114.3, -908.05) * mm, "radius": 2.38 * mm});
            skCircle(sketch, "E8.0.19.36", {"center": v(-114.3, -933.45) * mm, "radius": 2.38 * mm});
            skCircle(sketch, "E8.0.19.37", {"center": v(-114.3, -958.85) * mm, "radius": 2.38 * mm});
            skCircle(sketch, "E8.0.19.38", {"center": v(-114.3, -984.25) * mm, "radius": 2.38 * mm});
            skCircle(sketch, "E8.0.19.39", {"center": v(-114.3, -1009.65) * mm, "radius": 2.38 * mm});
            skCircle(sketch, "E8.0.19.40", {"center": v(-114.3, -1035.05) * mm, "radius": 2.38 * mm});
            skCircle(sketch, "E8.0.19.41", {"center": v(-114.3, -1060.45) * mm, "radius": 2.38 * mm});
            skCircle(sketch, "E8.0.19.42", {"center": v(-114.3, -1085.85) * mm, "radius": 2.38 * mm});
            skCircle(sketch, "E8.0.19.43", {"center": v(-114.3, -1111.25) * mm, "radius": 2.38 * mm});
            skCircle(sketch, "E8.0.19.44", {"center": v(-114.3, -1136.65) * mm, "radius": 2.38 * mm});
            skCircle(sketch, "E8.0.19.45", {"center": v(-114.3, -1162.05) * mm, "radius": 2.38 * mm});
            skCircle(sketch, "E8.0.20.25", {"center": v(-88.9, -654.05) * mm, "radius": 2.38 * mm});
            skCircle(sketch, "E8.0.20.26", {"center": v(-88.9, -679.45) * mm, "radius": 2.38 * mm});
            skCircle(sketch, "E8.0.20.27", {"center": v(-88.9, -704.85) * mm, "radius": 2.38 * mm});
            skCircle(sketch, "E8.0.20.28", {"center": v(-88.9, -730.25) * mm, "radius": 2.38 * mm});
            skCircle(sketch, "E8.0.20.29", {"center": v(-88.9, -755.65) * mm, "radius": 2.38 * mm});
            skCircle(sketch, "E8.0.20.30", {"center": v(-88.9, -781.05) * mm, "radius": 2.38 * mm});
            skCircle(sketch, "E8.0.20.31", {"center": v(-88.9, -806.45) * mm, "radius": 2.38 * mm});
            skCircle(sketch, "E8.0.20.32", {"center": v(-88.9, -831.85) * mm, "radius": 2.38 * mm});
            skCircle(sketch, "E8.0.20.33", {"center": v(-88.9, -857.25) * mm, "radius": 2.38 * mm});
            skCircle(sketch, "E8.0.20.34", {"center": v(-88.9, -882.65) * mm, "radius": 2.38 * mm});
            skCircle(sketch, "E8.0.20.35", {"center": v(-88.9, -908.05) * mm, "radius": 2.38 * mm});
            skCircle(sketch, "E8.0.20.36", {"center": v(-88.9, -933.45) * mm, "radius": 2.38 * mm});
            skCircle(sketch, "E8.0.20.37", {"center": v(-88.9, -958.85) * mm, "radius": 2.38 * mm});
            skCircle(sketch, "E8.0.20.38", {"center": v(-88.9, -984.25) * mm, "radius": 2.38 * mm});
            skCircle(sketch, "E8.0.20.39", {"center": v(-88.9, -1009.65) * mm, "radius": 2.38 * mm});
            skCircle(sketch, "E8.0.20.40", {"center": v(-88.9, -1035.05) * mm, "radius": 2.38 * mm});
            skCircle(sketch, "E8.0.20.41", {"center": v(-88.9, -1060.45) * mm, "radius": 2.38 * mm});
            skCircle(sketch, "E8.0.20.42", {"center": v(-88.9, -1085.85) * mm, "radius": 2.38 * mm});
            skCircle(sketch, "E8.0.20.43", {"center": v(-88.9, -1111.25) * mm, "radius": 2.38 * mm});
            skCircle(sketch, "E8.0.20.44", {"center": v(-88.9, -1136.65) * mm, "radius": 2.38 * mm});
            skCircle(sketch, "E8.0.20.45", {"center": v(-88.9, -1162.05) * mm, "radius": 2.38 * mm});
            skCircle(sketch, "E8.0.21.25", {"center": v(-63.5, -654.05) * mm, "radius": 2.38 * mm});
            skCircle(sketch, "E8.0.21.26", {"center": v(-63.5, -679.45) * mm, "radius": 2.38 * mm});
            skCircle(sketch, "E8.0.21.27", {"center": v(-63.5, -704.85) * mm, "radius": 2.38 * mm});
            skCircle(sketch, "E8.0.21.28", {"center": v(-63.5, -730.25) * mm, "radius": 2.38 * mm});
            skCircle(sketch, "E8.0.21.29", {"center": v(-63.5, -755.65) * mm, "radius": 2.38 * mm});
            skCircle(sketch, "E8.0.21.30", {"center": v(-63.5, -781.05) * mm, "radius": 2.38 * mm});
            skCircle(sketch, "E8.0.21.31", {"center": v(-63.5, -806.45) * mm, "radius": 2.38 * mm});
            skCircle(sketch, "E8.0.21.32", {"center": v(-63.5, -831.85) * mm, "radius": 2.38 * mm});
            skCircle(sketch, "E8.0.21.33", {"center": v(-63.5, -857.25) * mm, "radius": 2.38 * mm});
            skCircle(sketch, "E8.0.21.34", {"center": v(-63.5, -882.65) * mm, "radius": 2.38 * mm});
            skCircle(sketch, "E8.0.21.35", {"center": v(-63.5, -908.05) * mm, "radius": 2.38 * mm});
            skCircle(sketch, "E8.0.21.36", {"center": v(-63.5, -933.45) * mm, "radius": 2.38 * mm});
            skCircle(sketch, "E8.0.21.37", {"center": v(-63.5, -958.85) * mm, "radius": 2.38 * mm});
            skCircle(sketch, "E8.0.21.38", {"center": v(-63.5, -984.25) * mm, "radius": 2.38 * mm});
            skCircle(sketch, "E8.0.21.39", {"center": v(-63.5, -1009.65) * mm, "radius": 2.38 * mm});
            skCircle(sketch, "E8.0.21.40", {"center": v(-63.5, -1035.05) * mm, "radius": 2.38 * mm});
            skCircle(sketch, "E8.0.21.41", {"center": v(-63.5, -1060.45) * mm, "radius": 2.38 * mm});
            skCircle(sketch, "E8.0.21.42", {"center": v(-63.5, -1085.85) * mm, "radius": 2.38 * mm});
            skCircle(sketch, "E8.0.21.43", {"center": v(-63.5, -1111.25) * mm, "radius": 2.38 * mm});
            skCircle(sketch, "E8.0.21.44", {"center": v(-63.5, -1136.65) * mm, "radius": 2.38 * mm});
            skCircle(sketch, "E8.0.21.45", {"center": v(-63.5, -1162.05) * mm, "radius": 2.38 * mm});
            skCircle(sketch, "E8.0.22.25", {"center": v(-38.1, -654.05) * mm, "radius": 2.38 * mm});
            skCircle(sketch, "E8.0.22.26", {"center": v(-38.1, -679.45) * mm, "radius": 2.38 * mm});
            skCircle(sketch, "E8.0.22.27", {"center": v(-38.1, -704.85) * mm, "radius": 2.38 * mm});
            skCircle(sketch, "E8.0.22.28", {"center": v(-38.1, -730.25) * mm, "radius": 2.38 * mm});
            skCircle(sketch, "E8.0.22.29", {"center": v(-38.1, -755.65) * mm, "radius": 2.38 * mm});
            skCircle(sketch, "E8.0.22.30", {"center": v(-38.1, -781.05) * mm, "radius": 2.38 * mm});
            skCircle(sketch, "E8.0.22.31", {"center": v(-38.1, -806.45) * mm, "radius": 2.38 * mm});
            skCircle(sketch, "E8.0.22.32", {"center": v(-38.1, -831.85) * mm, "radius": 2.38 * mm});
            skCircle(sketch, "E8.0.22.33", {"center": v(-38.1, -857.25) * mm, "radius": 2.38 * mm});
            skCircle(sketch, "E8.0.22.34", {"center": v(-38.1, -882.65) * mm, "radius": 2.38 * mm});
            skCircle(sketch, "E8.0.22.35", {"center": v(-38.1, -908.05) * mm, "radius": 2.38 * mm});
            skCircle(sketch, "E8.0.22.36", {"center": v(-38.1, -933.45) * mm, "radius": 2.38 * mm});
            skCircle(sketch, "E8.0.22.37", {"center": v(-38.1, -958.85) * mm, "radius": 2.38 * mm});
            skCircle(sketch, "E8.0.22.38", {"center": v(-38.1, -984.25) * mm, "radius": 2.38 * mm});
            skCircle(sketch, "E8.0.22.39", {"center": v(-38.1, -1009.65) * mm, "radius": 2.38 * mm});
            skCircle(sketch, "E8.0.22.40", {"center": v(-38.1, -1035.05) * mm, "radius": 2.38 * mm});
            skCircle(sketch, "E8.0.22.41", {"center": v(-38.1, -1060.45) * mm, "radius": 2.38 * mm});
            skCircle(sketch, "E8.0.22.42", {"center": v(-38.1, -1085.85) * mm, "radius": 2.38 * mm});
            skCircle(sketch, "E8.0.22.43", {"center": v(-38.1, -1111.25) * mm, "radius": 2.38 * mm});
            skCircle(sketch, "E8.0.22.44", {"center": v(-38.1, -1136.65) * mm, "radius": 2.38 * mm});
            skCircle(sketch, "E8.0.22.45", {"center": v(-38.1, -1162.05) * mm, "radius": 2.38 * mm});
            skCircle(sketch, "E8.0.23.25", {"center": v(-12.7, -654.05) * mm, "radius": 2.38 * mm});
            skCircle(sketch, "E8.0.23.26", {"center": v(-12.7, -679.45) * mm, "radius": 2.38 * mm});
            skCircle(sketch, "E8.0.23.27", {"center": v(-12.7, -704.85) * mm, "radius": 2.38 * mm});
            skCircle(sketch, "E8.0.23.28", {"center": v(-12.7, -730.25) * mm, "radius": 2.38 * mm});
            skCircle(sketch, "E8.0.23.29", {"center": v(-12.7, -755.65) * mm, "radius": 2.38 * mm});
            skCircle(sketch, "E8.0.23.30", {"center": v(-12.7, -781.05) * mm, "radius": 2.38 * mm});
            skCircle(sketch, "E8.0.23.31", {"center": v(-12.7, -806.45) * mm, "radius": 2.38 * mm});
            skCircle(sketch, "E8.0.23.32", {"center": v(-12.7, -831.85) * mm, "radius": 2.38 * mm});
            skCircle(sketch, "E8.0.23.33", {"center": v(-12.7, -857.25) * mm, "radius": 2.38 * mm});
            skCircle(sketch, "E8.0.23.34", {"center": v(-12.7, -882.65) * mm, "radius": 2.38 * mm});
            skCircle(sketch, "E8.0.23.35", {"center": v(-12.7, -908.05) * mm, "radius": 2.38 * mm});
            skCircle(sketch, "E8.0.23.36", {"center": v(-12.7, -933.45) * mm, "radius": 2.38 * mm});
            skCircle(sketch, "E8.0.23.37", {"center": v(-12.7, -958.85) * mm, "radius": 2.38 * mm});
            skCircle(sketch, "E8.0.23.38", {"center": v(-12.7, -984.25) * mm, "radius": 2.38 * mm});
            skCircle(sketch, "E8.0.23.39", {"center": v(-12.7, -1009.65) * mm, "radius": 2.38 * mm});
            skCircle(sketch, "E8.0.23.40", {"center": v(-12.7, -1035.05) * mm, "radius": 2.38 * mm});
            skCircle(sketch, "E8.0.23.41", {"center": v(-12.7, -1060.45) * mm, "radius": 2.38 * mm});
            skCircle(sketch, "E8.0.23.42", {"center": v(-12.7, -1085.85) * mm, "radius": 2.38 * mm});
            skCircle(sketch, "E8.0.23.43", {"center": v(-12.7, -1111.25) * mm, "radius": 2.38 * mm});
            skCircle(sketch, "E8.0.23.44", {"center": v(-12.7, -1136.65) * mm, "radius": 2.38 * mm});
            skCircle(sketch, "E8.0.23.45", {"center": v(-12.7, -1162.05) * mm, "radius": 2.38 * mm});
            skSolve(sketch);
        }
        {
            var Q0;
            Q0=makeQuery(id+"F0.imprint","IMPRINT",FACE,{"disambiguationData":[TD([[makeQuery(id+"F0.imprint","IMPRINT",EDGE,{"derivedFrom":sQuery(id+"F0.wireOp",EDGE,"E0.bottom")}),-1.0]])]});
            extrude(context, id + "F1", {"entities" : qUnion([Q0]), "depth" : 3.17 * mm});
        }
    });
